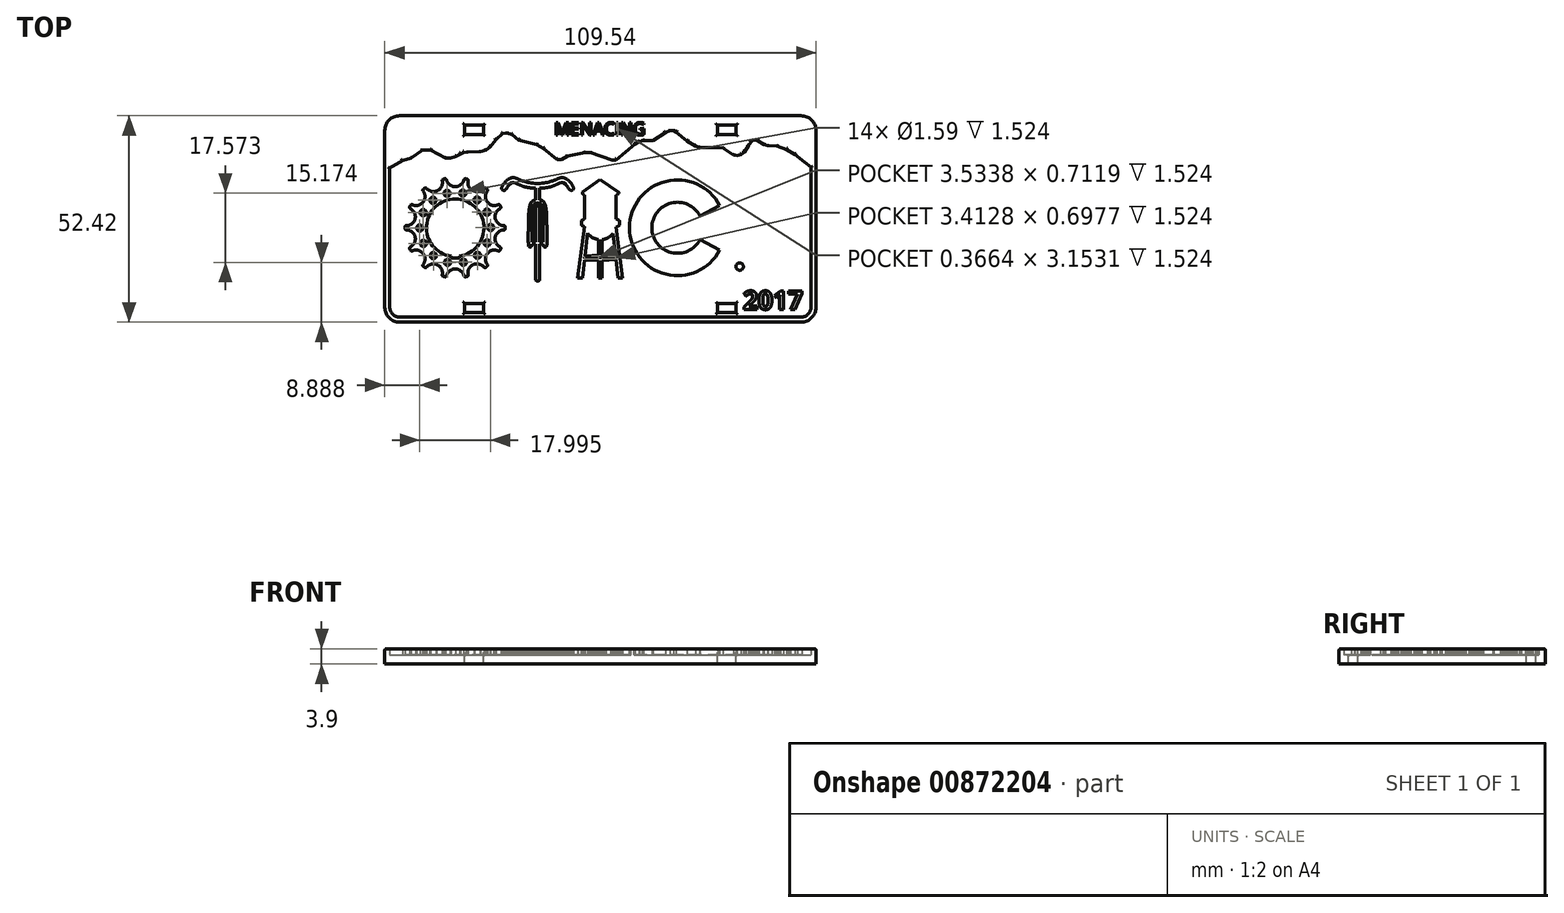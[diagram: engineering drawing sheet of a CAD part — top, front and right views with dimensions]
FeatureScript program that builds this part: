
annotation { "Feature Type Name" : "Feature", "Feature Type Description" : "" }
export const myFeature = defineFeature(function(context is Context, id is Id, definition is map)
    precondition{}
    {
        {
            var Q0;
            Q0=qCreatedBy(makeId("Top.planeOp"),FACE);
            var sketch = newSketch(context, id + "F0", { "sketchPlane" : qUnion([Q0])});
            skLineSegment(sketch, "E0", {"start": v(54.77, -22.46) * mm, "end": v(54.77, 22.46) * mm});
            skArc(sketch, "E1", {"start": v(54.77, 22.46) * mm, "mid": v(53.68, 25.11) * mm, "end": v(51.02, 26.21) * mm});
            skLineSegment(sketch, "E2", {"start": v(51.02, 26.21) * mm, "end": v(-51.02, 26.21) * mm});
            skArc(sketch, "E3", {"start": v(-51.02, 26.21) * mm, "mid": v(-53.68, 25.11) * mm, "end": v(-54.77, 22.46) * mm});
            skLineSegment(sketch, "E4", {"start": v(-54.77, 22.46) * mm, "end": v(-54.77, -22.46) * mm});
            skArc(sketch, "E5", {"start": v(-54.77, -22.46) * mm, "mid": v(-53.54, -25.24) * mm, "end": v(-50.64, -26.2) * mm});
            skLineSegment(sketch, "E6", {"start": v(-50.64, -26.2) * mm, "end": v(51.04, -26.2) * mm});
            skArc(sketch, "E7", {"start": v(51.02, -26.21) * mm, "mid": v(53.68, -25.11) * mm, "end": v(54.77, -22.46) * mm});
            skLineSegment(sketch, "E8", {"start": v(-54.77, 12.13) * mm, "end": v(-50.31, 14.84) * mm});
            skLineSegment(sketch, "E9", {"start": v(-50.31, 14.84) * mm, "end": v(-48.06, 15.4) * mm});
            skLineSegment(sketch, "E10", {"start": v(-48.06, 15.4) * mm, "end": v(-45.2, 17.44) * mm});
            skLineSegment(sketch, "E11", {"start": v(-45.2, 17.44) * mm, "end": v(-43.14, 17.44) * mm});
            skLineSegment(sketch, "E12", {"start": v(-43.14, 17.44) * mm, "end": v(-39.3, 15.5) * mm});
            skLineSegment(sketch, "E13", {"start": v(-39.3, 15.5) * mm, "end": v(-38.03, 15.49) * mm});
            skLineSegment(sketch, "E14", {"start": v(-38.03, 15.49) * mm, "end": v(-36.75, 15.8) * mm});
            skLineSegment(sketch, "E15", {"start": v(-36.75, 15.8) * mm, "end": v(-35.57, 16.54) * mm});
            skLineSegment(sketch, "E16", {"start": v(-35.57, 16.54) * mm, "end": v(-34.73, 16.88) * mm});
            skLineSegment(sketch, "E17", {"start": v(-34.73, 16.88) * mm, "end": v(-33.6, 17.01) * mm});
            skLineSegment(sketch, "E18", {"start": v(-33.6, 17.01) * mm, "end": v(-30.43, 17.11) * mm});
            skLineSegment(sketch, "E19", {"start": v(-30.43, 17.11) * mm, "end": v(-29.05, 17.5) * mm});
            skLineSegment(sketch, "E20", {"start": v(-29.05, 17.5) * mm, "end": v(-27.98, 18.27) * mm});
            skLineSegment(sketch, "E21", {"start": v(-27.98, 18.27) * mm, "end": v(-26.53, 20.14) * mm});
            skLineSegment(sketch, "E22", {"start": v(-26.53, 20.14) * mm, "end": v(-24.88, 21.63) * mm});
            skLineSegment(sketch, "E23", {"start": v(-24.88, 21.63) * mm, "end": v(-23.73, 21.77) * mm});
            skLineSegment(sketch, "E24", {"start": v(-23.73, 21.77) * mm, "end": v(-22.5, 21.4) * mm});
            skLineSegment(sketch, "E25", {"start": v(-22.5, 21.4) * mm, "end": v(-20.72, 20.04) * mm});
            skLineSegment(sketch, "E26", {"start": v(-20.72, 20.04) * mm, "end": v(-16.23, 18.87) * mm});
            skLineSegment(sketch, "E27", {"start": v(-16.23, 18.87) * mm, "end": v(-14.45, 17.85) * mm});
            skLineSegment(sketch, "E28", {"start": v(-14.45, 17.85) * mm, "end": v(-11.02, 15.1) * mm});
            skLineSegment(sketch, "E29", {"start": v(-11.02, 15.1) * mm, "end": v(-9.93, 15.1) * mm});
            skLineSegment(sketch, "E30", {"start": v(-9.93, 15.1) * mm, "end": v(-8.4, 15.96) * mm});
            skLineSegment(sketch, "E31", {"start": v(-8.4, 15.96) * mm, "end": v(-3.94, 16.85) * mm});
            skLineSegment(sketch, "E32", {"start": v(-3.94, 16.85) * mm, "end": v(-2.54, 16.85) * mm});
            skLineSegment(sketch, "E33", {"start": v(-2.54, 16.85) * mm, "end": v(2.9, 14.97) * mm});
            skLineSegment(sketch, "E34", {"start": v(2.9, 14.97) * mm, "end": v(3.92, 14.97) * mm});
            skLineSegment(sketch, "E35", {"start": v(3.92, 14.97) * mm, "end": v(8.8, 18.97) * mm});
            skLineSegment(sketch, "E36", {"start": v(8.8, 18.97) * mm, "end": v(9.82, 19.64) * mm});
            skLineSegment(sketch, "E37", {"start": v(9.82, 19.64) * mm, "end": v(10.9, 19.97) * mm});
            skLineSegment(sketch, "E38", {"start": v(10.9, 19.97) * mm, "end": v(13.43, 19.86) * mm});
            skLineSegment(sketch, "E39", {"start": v(13.43, 19.86) * mm, "end": v(16.5, 21.96) * mm});
            skLineSegment(sketch, "E40", {"start": v(16.5, 21.96) * mm, "end": v(17.71, 22.42) * mm});
            skLineSegment(sketch, "E41", {"start": v(17.71, 22.42) * mm, "end": v(18.56, 22.45) * mm});
            skLineSegment(sketch, "E42", {"start": v(18.56, 22.45) * mm, "end": v(19.28, 22.13) * mm});
            skLineSegment(sketch, "E43", {"start": v(19.28, 22.13) * mm, "end": v(22.05, 19.8) * mm});
            skLineSegment(sketch, "E44", {"start": v(22.05, 19.8) * mm, "end": v(24.2, 18.5) * mm});
            skLineSegment(sketch, "E45", {"start": v(24.2, 18.5) * mm, "end": v(25.23, 18.2) * mm});
            skLineSegment(sketch, "E46", {"start": v(25.23, 18.2) * mm, "end": v(29.85, 18.2) * mm});
            skLineSegment(sketch, "E47", {"start": v(29.85, 18.2) * mm, "end": v(31.13, 17.95) * mm});
            skLineSegment(sketch, "E48", {"start": v(31.13, 17.95) * mm, "end": v(33.84, 16.27) * mm});
            skLineSegment(sketch, "E49", {"start": v(33.84, 16.27) * mm, "end": v(34.73, 16.06) * mm});
            skLineSegment(sketch, "E50", {"start": v(34.73, 16.06) * mm, "end": v(35.67, 16.3) * mm});
            skLineSegment(sketch, "E51", {"start": v(35.67, 16.3) * mm, "end": v(36.58, 16.95) * mm});
            skLineSegment(sketch, "E52", {"start": v(36.58, 16.95) * mm, "end": v(37.58, 18.67) * mm});
            skLineSegment(sketch, "E53", {"start": v(37.58, 18.67) * mm, "end": v(38.22, 19.58) * mm});
            skLineSegment(sketch, "E54", {"start": v(38.22, 19.58) * mm, "end": v(38.96, 20.06) * mm});
            skLineSegment(sketch, "E55", {"start": v(38.96, 20.06) * mm, "end": v(39.94, 19.92) * mm});
            skLineSegment(sketch, "E56", {"start": v(39.94, 19.92) * mm, "end": v(41.58, 18.88) * mm});
            skLineSegment(sketch, "E57", {"start": v(41.58, 18.88) * mm, "end": v(42.4, 18.61) * mm});
            skLineSegment(sketch, "E58", {"start": v(42.4, 18.61) * mm, "end": v(44.9, 18.47) * mm});
            skLineSegment(sketch, "E59", {"start": v(44.9, 18.47) * mm, "end": v(47.31, 17.68) * mm});
            skLineSegment(sketch, "E60", {"start": v(47.31, 17.68) * mm, "end": v(49.47, 16.33) * mm});
            skLineSegment(sketch, "E61", {"start": v(49.47, 16.33) * mm, "end": v(51.88, 14.42) * mm});
            skLineSegment(sketch, "E62", {"start": v(51.88, 14.42) * mm, "end": v(53.78, 12.92) * mm});
            skLineSegment(sketch, "E63", {"start": v(53.78, 12.92) * mm, "end": v(54.77, 12.06) * mm});
            skArc(sketch, "E64", {"start": v(-33.82, 10.1) * mm, "mid": v(-34.05, 10.15) * mm, "end": v(-34.28, 10.2) * mm});
            skArc(sketch, "E65", {"start": v(-33.6, 9.72) * mm, "mid": v(-33.63, 9.96) * mm, "end": v(-33.82, 10.1) * mm});
            skArc(sketch, "E66", {"start": v(-39.11, 9.96) * mm, "mid": v(-36.88, 8.19) * mm, "end": v(-34.66, 9.96) * mm});
            skArc(sketch, "E67", {"start": v(-34.28, 10.2) * mm, "mid": v(-34.52, 10.16) * mm, "end": v(-34.66, 9.96) * mm});
            skArc(sketch, "E68", {"start": v(-39.49, 10.2) * mm, "mid": v(-39.72, 10.15) * mm, "end": v(-39.94, 10.1) * mm});
            skArc(sketch, "E69", {"start": v(-39.11, 9.96) * mm, "mid": v(-39.25, 10.16) * mm, "end": v(-39.49, 10.2) * mm});
            skArc(sketch, "E70", {"start": v(-44.19, 7.79) * mm, "mid": v(-41.41, 7.16) * mm, "end": v(-40.18, 9.72) * mm});
            skArc(sketch, "E71", {"start": v(-39.94, 10.1) * mm, "mid": v(-40.14, 9.96) * mm, "end": v(-40.18, 9.72) * mm});
            skArc(sketch, "E72", {"start": v(-44.63, 7.84) * mm, "mid": v(-44.82, 7.7) * mm, "end": v(-45, 7.55) * mm});
            skArc(sketch, "E73", {"start": v(-44.19, 7.79) * mm, "mid": v(-44.4, 7.9) * mm, "end": v(-44.63, 7.84) * mm});
            skArc(sketch, "E74", {"start": v(-47.82, 3.63) * mm, "mid": v(-45.05, 4.26) * mm, "end": v(-45.05, 7.1) * mm});
            skArc(sketch, "E75", {"start": v(-45, 7.55) * mm, "mid": v(-45.11, 7.34) * mm, "end": v(-45.05, 7.1) * mm});
            skArc(sketch, "E76", {"start": v(-48.24, 3.48) * mm, "mid": v(-48.35, 3.27) * mm, "end": v(-48.45, 3.06) * mm});
            skArc(sketch, "E77", {"start": v(-47.82, 3.63) * mm, "mid": v(-48.06, 3.64) * mm, "end": v(-48.24, 3.48) * mm});
            skArc(sketch, "E78", {"start": v(-49.29, -1.7) * mm, "mid": v(-47.06, 0.07) * mm, "end": v(-48.3, 2.64) * mm});
            skArc(sketch, "E79", {"start": v(-48.45, 3.06) * mm, "mid": v(-48.46, 2.82) * mm, "end": v(-48.3, 2.64) * mm});
            skArc(sketch, "E80", {"start": v(-49.6, -2.01) * mm, "mid": v(-49.6, -2.25) * mm, "end": v(-49.6, -2.48) * mm});
            skArc(sketch, "E81", {"start": v(-49.29, -1.7) * mm, "mid": v(-49.5, -1.8) * mm, "end": v(-49.6, -2.01) * mm});
            skArc(sketch, "E82", {"start": v(-48.3, -7.14) * mm, "mid": v(-47.06, -4.57) * mm, "end": v(-49.29, -2.8) * mm});
            skArc(sketch, "E83", {"start": v(-49.6, -2.48) * mm, "mid": v(-49.5, -2.7) * mm, "end": v(-49.29, -2.8) * mm});
            skArc(sketch, "E84", {"start": v(-48.45, -7.56) * mm, "mid": v(-48.35, -7.77) * mm, "end": v(-48.24, -7.98) * mm});
            skArc(sketch, "E85", {"start": v(-48.3, -7.14) * mm, "mid": v(-48.46, -7.32) * mm, "end": v(-48.45, -7.56) * mm});
            skArc(sketch, "E86", {"start": v(-45.05, -11.6) * mm, "mid": v(-45.05, -8.76) * mm, "end": v(-47.82, -8.12) * mm});
            skArc(sketch, "E87", {"start": v(-48.24, -7.98) * mm, "mid": v(-48.06, -8.14) * mm, "end": v(-47.82, -8.12) * mm});
            skArc(sketch, "E88", {"start": v(-45, -12.05) * mm, "mid": v(-44.82, -12.2) * mm, "end": v(-44.63, -12.34) * mm});
            skArc(sketch, "E89", {"start": v(-45.05, -11.6) * mm, "mid": v(-45.11, -11.84) * mm, "end": v(-45, -12.05) * mm});
            skArc(sketch, "E90", {"start": v(-40.18, -14.22) * mm, "mid": v(-41.41, -11.65) * mm, "end": v(-44.19, -12.29) * mm});
            skArc(sketch, "E91", {"start": v(-44.63, -12.34) * mm, "mid": v(-44.4, -12.4) * mm, "end": v(-44.19, -12.29) * mm});
            skArc(sketch, "E92", {"start": v(-39.94, -14.6) * mm, "mid": v(-39.72, -14.65) * mm, "end": v(-39.49, -14.7) * mm});
            skArc(sketch, "E93", {"start": v(-40.18, -14.22) * mm, "mid": v(-40.14, -14.46) * mm, "end": v(-39.94, -14.6) * mm});
            skArc(sketch, "E94", {"start": v(-34.66, -14.46) * mm, "mid": v(-36.88, -12.69) * mm, "end": v(-39.11, -14.46) * mm});
            skArc(sketch, "E95", {"start": v(-39.49, -14.7) * mm, "mid": v(-39.25, -14.66) * mm, "end": v(-39.11, -14.46) * mm});
            skArc(sketch, "E96", {"start": v(-34.28, -14.7) * mm, "mid": v(-34.05, -14.65) * mm, "end": v(-33.82, -14.6) * mm});
            skArc(sketch, "E97", {"start": v(-34.66, -14.46) * mm, "mid": v(-34.52, -14.66) * mm, "end": v(-34.28, -14.7) * mm});
            skArc(sketch, "E98", {"start": v(-29.58, -12.29) * mm, "mid": v(-32.36, -11.65) * mm, "end": v(-33.6, -14.22) * mm});
            skArc(sketch, "E99", {"start": v(-33.82, -14.6) * mm, "mid": v(-33.63, -14.46) * mm, "end": v(-33.6, -14.22) * mm});
            skArc(sketch, "E100", {"start": v(-29.14, -12.34) * mm, "mid": v(-28.95, -12.2) * mm, "end": v(-28.77, -12.05) * mm});
            skArc(sketch, "E101", {"start": v(-29.58, -12.29) * mm, "mid": v(-29.37, -12.4) * mm, "end": v(-29.14, -12.34) * mm});
            skArc(sketch, "E102", {"start": v(-25.95, -8.12) * mm, "mid": v(-28.72, -8.76) * mm, "end": v(-28.72, -11.6) * mm});
            skArc(sketch, "E103", {"start": v(-28.77, -12.05) * mm, "mid": v(-28.66, -11.84) * mm, "end": v(-28.72, -11.6) * mm});
            skArc(sketch, "E104", {"start": v(-25.53, -7.98) * mm, "mid": v(-25.42, -7.77) * mm, "end": v(-25.32, -7.56) * mm});
            skArc(sketch, "E105", {"start": v(-25.95, -8.12) * mm, "mid": v(-25.7, -8.14) * mm, "end": v(-25.53, -7.98) * mm});
            skArc(sketch, "E106", {"start": v(-24.48, -2.8) * mm, "mid": v(-26.7, -4.57) * mm, "end": v(-25.47, -7.14) * mm});
            skArc(sketch, "E107", {"start": v(-25.32, -7.56) * mm, "mid": v(-25.31, -7.32) * mm, "end": v(-25.47, -7.14) * mm});
            skArc(sketch, "E108", {"start": v(-24.16, -2.48) * mm, "mid": v(-24.16, -2.25) * mm, "end": v(-24.16, -2.01) * mm});
            skArc(sketch, "E109", {"start": v(-24.48, -2.8) * mm, "mid": v(-24.26, -2.7) * mm, "end": v(-24.16, -2.48) * mm});
            skArc(sketch, "E110", {"start": v(-25.47, 2.64) * mm, "mid": v(-26.7, 0.07) * mm, "end": v(-24.48, -1.7) * mm});
            skArc(sketch, "E111", {"start": v(-24.16, -2.01) * mm, "mid": v(-24.26, -1.8) * mm, "end": v(-24.48, -1.7) * mm});
            skArc(sketch, "E112", {"start": v(-25.32, 3.06) * mm, "mid": v(-25.42, 3.27) * mm, "end": v(-25.53, 3.48) * mm});
            skArc(sketch, "E113", {"start": v(-25.47, 2.64) * mm, "mid": v(-25.31, 2.82) * mm, "end": v(-25.32, 3.06) * mm});
            skArc(sketch, "E114", {"start": v(-28.72, 7.1) * mm, "mid": v(-28.72, 4.26) * mm, "end": v(-25.95, 3.63) * mm});
            skArc(sketch, "E115", {"start": v(-25.53, 3.48) * mm, "mid": v(-25.7, 3.64) * mm, "end": v(-25.95, 3.63) * mm});
            skArc(sketch, "E116", {"start": v(-28.77, 7.55) * mm, "mid": v(-28.95, 7.7) * mm, "end": v(-29.14, 7.84) * mm});
            skArc(sketch, "E117", {"start": v(-28.72, 7.1) * mm, "mid": v(-28.66, 7.34) * mm, "end": v(-28.77, 7.55) * mm});
            skArc(sketch, "E118", {"start": v(-33.6, 9.72) * mm, "mid": v(-32.36, 7.16) * mm, "end": v(-29.58, 7.79) * mm});
            skArc(sketch, "E119", {"start": v(-29.14, 7.84) * mm, "mid": v(-29.37, 7.9) * mm, "end": v(-29.58, 7.79) * mm});
            skArc(sketch, "E120", {"start": v(-35.84, -9.47) * mm, "mid": v(-36.88, 5.05) * mm, "end": v(-37.93, -9.47) * mm});
            skCircle(sketch, "E121", {"center": v(19.55, -2.25) * mm, "radius": 4.78 * mm});
            skLineSegment(sketch, "E122", {"start": v(25.28, 0.76) * mm, "end": v(30.31, 3.41) * mm});
            skArc(sketch, "E123", {"start": v(30.31, 3.41) * mm, "mid": v(7.4, -2.25) * mm, "end": v(30.31, -7.9) * mm});
            skLineSegment(sketch, "E124", {"start": v(25.28, -5.26) * mm, "end": v(30.31, -7.9) * mm});
            skLineSegment(sketch, "E125", {"start": v(5.68, -15.07) * mm, "end": v(3.96, -2.08) * mm});
            skLineSegment(sketch, "E126", {"start": v(4.46, -15.07) * mm, "end": v(3.92, -10.33) * mm});
            skLineSegment(sketch, "E127", {"start": v(3.83, -9.95) * mm, "end": v(3.8, -9.64) * mm});
            skLineSegment(sketch, "E128", {"start": v(3.8, -9.28) * mm, "end": v(3.17, -3.74) * mm});
            skLineSegment(sketch, "E129", {"start": v(-0.06, 10.03) * mm, "end": v(4.72, 6.75) * mm});
            skLineSegment(sketch, "E130", {"start": v(-4.58, 6.82) * mm, "end": v(-0.06, 10.03) * mm});
            skLineSegment(sketch, "E131", {"start": v(3.92, -10.33) * mm, "end": v(0.42, -10.54) * mm});
            skLineSegment(sketch, "E132", {"start": v(-0.52, -10.52) * mm, "end": v(-4.03, -10.4) * mm});
            skLineSegment(sketch, "E133", {"start": v(-3.93, -9.37) * mm, "end": v(-0.52, -9.12) * mm});
            skLineSegment(sketch, "E134", {"start": v(0.42, -9.16) * mm, "end": v(3.8, -9.28) * mm});
            skLineSegment(sketch, "E135", {"start": v(3.83, -9.95) * mm, "end": v(0.42, -10.22) * mm});
            skLineSegment(sketch, "E136", {"start": v(-0.52, -10.17) * mm, "end": v(-4.05, -10.05) * mm});
            skLineSegment(sketch, "E137", {"start": v(-4.05, -10.05) * mm, "end": v(-3.98, -9.72) * mm});
            skLineSegment(sketch, "E138", {"start": v(-3.98, -9.72) * mm, "end": v(-0.52, -9.46) * mm});
            skLineSegment(sketch, "E139", {"start": v(0.42, -9.53) * mm, "end": v(3.8, -9.64) * mm});
            skLineSegment(sketch, "E140", {"start": v(3.94, 6.03) * mm, "end": v(4.02, -0.07) * mm});
            skLineSegment(sketch, "E141", {"start": v(-3.97, 6.02) * mm, "end": v(-3.96, -0.05) * mm});
            skLineSegment(sketch, "E142", {"start": v(4.85, -0.43) * mm, "end": v(4.82, -1.6) * mm});
            skLineSegment(sketch, "E143", {"start": v(-4.82, -0.4) * mm, "end": v(-4.8, -1.63) * mm});
            skArc(sketch, "E144", {"start": v(3.94, 6.03) * mm, "mid": v(4.44, 6.27) * mm, "end": v(4.72, 6.75) * mm});
            skArc(sketch, "E145", {"start": v(-4.58, 6.82) * mm, "mid": v(-4.44, 6.3) * mm, "end": v(-3.97, 6.02) * mm});
            skArc(sketch, "E146", {"start": v(4.85, -0.43) * mm, "mid": v(4.45, -0.2) * mm, "end": v(4.02, -0.07) * mm});
            skArc(sketch, "E147", {"start": v(-3.96, -0.05) * mm, "mid": v(-4.4, -0.19) * mm, "end": v(-4.82, -0.4) * mm});
            skArc(sketch, "E148", {"start": v(-4.8, -1.63) * mm, "mid": v(-4.43, -1.8) * mm, "end": v(-4.05, -1.93) * mm});
            skArc(sketch, "E149", {"start": v(3.96, -2.08) * mm, "mid": v(4.42, -1.9) * mm, "end": v(4.82, -1.6) * mm});
            skArc(sketch, "E150", {"start": v(-3.27, -3.62) * mm, "mid": v(-2.06, -4.7) * mm, "end": v(-0.52, -5.22) * mm});
            skArc(sketch, "E151", {"start": v(0.42, -5.23) * mm, "mid": v(1.94, -4.76) * mm, "end": v(3.17, -3.74) * mm});
            skLineSegment(sketch, "E152", {"start": v(-5.8, -15.07) * mm, "end": v(-4.05, -1.93) * mm});
            skLineSegment(sketch, "E153", {"start": v(-3.93, -9.37) * mm, "end": v(-3.27, -3.62) * mm});
            skLineSegment(sketch, "E154", {"start": v(-4.56, -15.07) * mm, "end": v(-4.03, -10.4) * mm});
            skLineSegment(sketch, "E155", {"start": v(-0.52, -5.22) * mm, "end": v(-0.52, -9.12) * mm});
            skLineSegment(sketch, "E156", {"start": v(-0.52, -10.52) * mm, "end": v(-0.52, -15.07) * mm});
            skLineSegment(sketch, "E157", {"start": v(0.42, -5.23) * mm, "end": v(0.42, -9.16) * mm});
            skLineSegment(sketch, "E158", {"start": v(0.42, -10.54) * mm, "end": v(0.42, -15.07) * mm});
            skLineSegment(sketch, "E159", {"start": v(-4.56, -15.07) * mm, "end": v(-5.8, -15.07) * mm});
            skLineSegment(sketch, "E160", {"start": v(0.42, -15.07) * mm, "end": v(-0.52, -15.07) * mm});
            skLineSegment(sketch, "E161", {"start": v(5.68, -15.07) * mm, "end": v(4.46, -15.07) * mm});
            skLineSegment(sketch, "E162", {"start": v(-15.96, 9) * mm, "end": v(-16.55, 9.03) * mm});
            skLineSegment(sketch, "E163", {"start": v(-16.55, 9.03) * mm, "end": v(-17.09, 9.08) * mm});
            skLineSegment(sketch, "E164", {"start": v(-17.09, 9.08) * mm, "end": v(-17.58, 9.14) * mm});
            skLineSegment(sketch, "E165", {"start": v(-17.58, 9.14) * mm, "end": v(-18.03, 9.21) * mm});
            skLineSegment(sketch, "E166", {"start": v(-18.03, 9.21) * mm, "end": v(-18.44, 9.3) * mm});
            skLineSegment(sketch, "E167", {"start": v(-18.44, 9.3) * mm, "end": v(-18.8, 9.39) * mm});
            skLineSegment(sketch, "E168", {"start": v(-18.8, 9.39) * mm, "end": v(-19.14, 9.48) * mm});
            skLineSegment(sketch, "E169", {"start": v(-19.14, 9.48) * mm, "end": v(-19.45, 9.57) * mm});
            skLineSegment(sketch, "E170", {"start": v(-19.45, 9.57) * mm, "end": v(-19.73, 9.67) * mm});
            skLineSegment(sketch, "E171", {"start": v(-19.73, 9.67) * mm, "end": v(-19.99, 9.76) * mm});
            skLineSegment(sketch, "E172", {"start": v(-19.99, 9.76) * mm, "end": v(-20.22, 9.85) * mm});
            skLineSegment(sketch, "E173", {"start": v(-20.22, 9.85) * mm, "end": v(-20.43, 9.93) * mm});
            skLineSegment(sketch, "E174", {"start": v(-20.43, 9.93) * mm, "end": v(-20.62, 10.01) * mm});
            skLineSegment(sketch, "E175", {"start": v(-20.62, 10.01) * mm, "end": v(-20.79, 10.09) * mm});
            skLineSegment(sketch, "E176", {"start": v(-20.79, 10.09) * mm, "end": v(-20.94, 10.15) * mm});
            skLineSegment(sketch, "E177", {"start": v(-20.94, 10.15) * mm, "end": v(-21.08, 10.22) * mm});
            skLineSegment(sketch, "E178", {"start": v(-21.08, 10.22) * mm, "end": v(-21.2, 10.27) * mm});
            skLineSegment(sketch, "E179", {"start": v(-21.2, 10.27) * mm, "end": v(-21.32, 10.32) * mm});
            skLineSegment(sketch, "E180", {"start": v(-21.32, 10.32) * mm, "end": v(-21.43, 10.35) * mm});
            skLineSegment(sketch, "E181", {"start": v(-21.43, 10.35) * mm, "end": v(-21.52, 10.39) * mm});
            skLineSegment(sketch, "E182", {"start": v(-21.52, 10.39) * mm, "end": v(-21.61, 10.42) * mm});
            skLineSegment(sketch, "E183", {"start": v(-21.61, 10.42) * mm, "end": v(-21.7, 10.44) * mm});
            skLineSegment(sketch, "E184", {"start": v(-21.7, 10.44) * mm, "end": v(-21.77, 10.46) * mm});
            skLineSegment(sketch, "E185", {"start": v(-21.77, 10.46) * mm, "end": v(-21.85, 10.47) * mm});
            skLineSegment(sketch, "E186", {"start": v(-21.85, 10.47) * mm, "end": v(-21.93, 10.48) * mm});
            skLineSegment(sketch, "E187", {"start": v(-21.93, 10.48) * mm, "end": v(-22, 10.5) * mm});
            skLineSegment(sketch, "E188", {"start": v(-22, 10.5) * mm, "end": v(-22.08, 10.5) * mm});
            skLineSegment(sketch, "E189", {"start": v(-22.08, 10.5) * mm, "end": v(-22.15, 10.5) * mm});
            skLineSegment(sketch, "E190", {"start": v(-22.15, 10.5) * mm, "end": v(-22.23, 10.5) * mm});
            skLineSegment(sketch, "E191", {"start": v(-22.23, 10.5) * mm, "end": v(-22.3, 10.5) * mm});
            skLineSegment(sketch, "E192", {"start": v(-22.3, 10.5) * mm, "end": v(-22.38, 10.48) * mm});
            skLineSegment(sketch, "E193", {"start": v(-22.38, 10.48) * mm, "end": v(-22.46, 10.47) * mm});
            skLineSegment(sketch, "E194", {"start": v(-22.46, 10.47) * mm, "end": v(-22.54, 10.46) * mm});
            skLineSegment(sketch, "E195", {"start": v(-22.54, 10.46) * mm, "end": v(-22.63, 10.44) * mm});
            skLineSegment(sketch, "E196", {"start": v(-22.63, 10.44) * mm, "end": v(-22.71, 10.41) * mm});
            skLineSegment(sketch, "E197", {"start": v(-22.71, 10.41) * mm, "end": v(-22.8, 10.39) * mm});
            skLineSegment(sketch, "E198", {"start": v(-22.8, 10.39) * mm, "end": v(-22.88, 10.36) * mm});
            skLineSegment(sketch, "E199", {"start": v(-22.88, 10.36) * mm, "end": v(-22.97, 10.32) * mm});
            skLineSegment(sketch, "E200", {"start": v(-22.97, 10.32) * mm, "end": v(-23.05, 10.28) * mm});
            skLineSegment(sketch, "E201", {"start": v(-23.05, 10.28) * mm, "end": v(-23.14, 10.24) * mm});
            skLineSegment(sketch, "E202", {"start": v(-23.14, 10.24) * mm, "end": v(-23.23, 10.2) * mm});
            skLineSegment(sketch, "E203", {"start": v(-23.23, 10.2) * mm, "end": v(-23.31, 10.14) * mm});
            skLineSegment(sketch, "E204", {"start": v(-23.31, 10.14) * mm, "end": v(-23.4, 10.09) * mm});
            skLineSegment(sketch, "E205", {"start": v(-23.4, 10.09) * mm, "end": v(-23.48, 10.03) * mm});
            skLineSegment(sketch, "E206", {"start": v(-23.48, 10.03) * mm, "end": v(-23.57, 9.97) * mm});
            skLineSegment(sketch, "E207", {"start": v(-23.57, 9.97) * mm, "end": v(-23.65, 9.9) * mm});
            skLineSegment(sketch, "E208", {"start": v(-23.65, 9.9) * mm, "end": v(-23.74, 9.83) * mm});
            skLineSegment(sketch, "E209", {"start": v(-23.74, 9.83) * mm, "end": v(-23.82, 9.76) * mm});
            skLineSegment(sketch, "E210", {"start": v(-23.82, 9.76) * mm, "end": v(-23.9, 9.7) * mm});
            skLineSegment(sketch, "E211", {"start": v(-23.9, 9.7) * mm, "end": v(-23.98, 9.62) * mm});
            skLineSegment(sketch, "E212", {"start": v(-23.98, 9.62) * mm, "end": v(-24.05, 9.54) * mm});
            skLineSegment(sketch, "E213", {"start": v(-24.05, 9.54) * mm, "end": v(-24.13, 9.45) * mm});
            skLineSegment(sketch, "E214", {"start": v(-24.13, 9.45) * mm, "end": v(-24.2, 9.36) * mm});
            skLineSegment(sketch, "E215", {"start": v(-24.2, 9.36) * mm, "end": v(-24.29, 9.27) * mm});
            skLineSegment(sketch, "E216", {"start": v(-24.29, 9.27) * mm, "end": v(-24.37, 9.17) * mm});
            skLineSegment(sketch, "E217", {"start": v(-24.37, 9.17) * mm, "end": v(-24.45, 9.06) * mm});
            skLineSegment(sketch, "E218", {"start": v(-24.45, 9.06) * mm, "end": v(-24.53, 8.94) * mm});
            skLineSegment(sketch, "E219", {"start": v(-24.53, 8.94) * mm, "end": v(-24.61, 8.82) * mm});
            skLineSegment(sketch, "E220", {"start": v(-24.61, 8.82) * mm, "end": v(-24.7, 8.7) * mm});
            skLineSegment(sketch, "E221", {"start": v(-24.7, 8.7) * mm, "end": v(-24.77, 8.57) * mm});
            skLineSegment(sketch, "E222", {"start": v(-24.77, 8.57) * mm, "end": v(-24.84, 8.45) * mm});
            skLineSegment(sketch, "E223", {"start": v(-24.84, 8.45) * mm, "end": v(-24.9, 8.33) * mm});
            skLineSegment(sketch, "E224", {"start": v(-24.9, 8.33) * mm, "end": v(-24.97, 8.22) * mm});
            skLineSegment(sketch, "E225", {"start": v(-24.97, 8.22) * mm, "end": v(-25.01, 8.11) * mm});
            skLineSegment(sketch, "E226", {"start": v(-25.01, 8.11) * mm, "end": v(-25.05, 8.02) * mm});
            skLineSegment(sketch, "E227", {"start": v(-25.05, 8.02) * mm, "end": v(-25.08, 7.94) * mm});
            skLineSegment(sketch, "E228", {"start": v(-25.08, 7.94) * mm, "end": v(-25.1, 7.87) * mm});
            skLineSegment(sketch, "E229", {"start": v(-25.1, 7.87) * mm, "end": v(-25.1, 7.8) * mm});
            skLineSegment(sketch, "E230", {"start": v(-25.1, 7.8) * mm, "end": v(-25.1, 7.74) * mm});
            skLineSegment(sketch, "E231", {"start": v(-25.1, 7.74) * mm, "end": v(-25.1, 7.7) * mm});
            skLineSegment(sketch, "E232", {"start": v(-25.1, 7.7) * mm, "end": v(-25.08, 7.64) * mm});
            skLineSegment(sketch, "E233", {"start": v(-25.08, 7.64) * mm, "end": v(-25.06, 7.6) * mm});
            skLineSegment(sketch, "E234", {"start": v(-25.06, 7.6) * mm, "end": v(-25.04, 7.55) * mm});
            skLineSegment(sketch, "E235", {"start": v(-25.04, 7.55) * mm, "end": v(-25, 7.5) * mm});
            skLineSegment(sketch, "E236", {"start": v(-25, 7.5) * mm, "end": v(-24.98, 7.47) * mm});
            skLineSegment(sketch, "E237", {"start": v(-24.98, 7.47) * mm, "end": v(-24.94, 7.43) * mm});
            skLineSegment(sketch, "E238", {"start": v(-24.94, 7.43) * mm, "end": v(-24.9, 7.4) * mm});
            skLineSegment(sketch, "E239", {"start": v(-24.9, 7.4) * mm, "end": v(-24.87, 7.36) * mm});
            skLineSegment(sketch, "E240", {"start": v(-24.87, 7.36) * mm, "end": v(-24.82, 7.34) * mm});
            skLineSegment(sketch, "E241", {"start": v(-24.82, 7.34) * mm, "end": v(-24.78, 7.31) * mm});
            skLineSegment(sketch, "E242", {"start": v(-24.78, 7.31) * mm, "end": v(-24.73, 7.3) * mm});
            skLineSegment(sketch, "E243", {"start": v(-24.73, 7.3) * mm, "end": v(-24.68, 7.28) * mm});
            skLineSegment(sketch, "E244", {"start": v(-24.68, 7.28) * mm, "end": v(-24.64, 7.27) * mm});
            skLineSegment(sketch, "E245", {"start": v(-24.64, 7.27) * mm, "end": v(-24.59, 7.26) * mm});
            skLineSegment(sketch, "E246", {"start": v(-24.59, 7.26) * mm, "end": v(-24.54, 7.26) * mm});
            skLineSegment(sketch, "E247", {"start": v(-24.54, 7.26) * mm, "end": v(-24.5, 7.26) * mm});
            skLineSegment(sketch, "E248", {"start": v(-24.5, 7.26) * mm, "end": v(-24.44, 7.26) * mm});
            skLineSegment(sketch, "E249", {"start": v(-24.44, 7.26) * mm, "end": v(-24.4, 7.27) * mm});
            skLineSegment(sketch, "E250", {"start": v(-24.4, 7.27) * mm, "end": v(-24.35, 7.28) * mm});
            skLineSegment(sketch, "E251", {"start": v(-24.35, 7.28) * mm, "end": v(-24.3, 7.3) * mm});
            skLineSegment(sketch, "E252", {"start": v(-24.3, 7.3) * mm, "end": v(-24.27, 7.3) * mm});
            skLineSegment(sketch, "E253", {"start": v(-24.27, 7.3) * mm, "end": v(-24.22, 7.33) * mm});
            skLineSegment(sketch, "E254", {"start": v(-24.22, 7.33) * mm, "end": v(-24.18, 7.36) * mm});
            skLineSegment(sketch, "E255", {"start": v(-24.18, 7.36) * mm, "end": v(-24.14, 7.4) * mm});
            skLineSegment(sketch, "E256", {"start": v(-24.14, 7.4) * mm, "end": v(-24.1, 7.43) * mm});
            skLineSegment(sketch, "E257", {"start": v(-24.1, 7.43) * mm, "end": v(-24.06, 7.48) * mm});
            skLineSegment(sketch, "E258", {"start": v(-24.06, 7.48) * mm, "end": v(-24.02, 7.53) * mm});
            skLineSegment(sketch, "E259", {"start": v(-24.02, 7.53) * mm, "end": v(-23.97, 7.59) * mm});
            skLineSegment(sketch, "E260", {"start": v(-23.97, 7.59) * mm, "end": v(-23.93, 7.65) * mm});
            skLineSegment(sketch, "E261", {"start": v(-23.93, 7.65) * mm, "end": v(-23.88, 7.72) * mm});
            skLineSegment(sketch, "E262", {"start": v(-23.88, 7.72) * mm, "end": v(-23.83, 7.8) * mm});
            skLineSegment(sketch, "E263", {"start": v(-23.83, 7.8) * mm, "end": v(-23.78, 7.87) * mm});
            skLineSegment(sketch, "E264", {"start": v(-23.78, 7.87) * mm, "end": v(-23.72, 7.96) * mm});
            skLineSegment(sketch, "E265", {"start": v(-23.72, 7.96) * mm, "end": v(-23.67, 8.04) * mm});
            skLineSegment(sketch, "E266", {"start": v(-23.67, 8.04) * mm, "end": v(-23.6, 8.13) * mm});
            skLineSegment(sketch, "E267", {"start": v(-23.6, 8.13) * mm, "end": v(-23.54, 8.23) * mm});
            skLineSegment(sketch, "E268", {"start": v(-23.54, 8.23) * mm, "end": v(-23.47, 8.32) * mm});
            skLineSegment(sketch, "E269", {"start": v(-23.47, 8.32) * mm, "end": v(-23.4, 8.41) * mm});
            skLineSegment(sketch, "E270", {"start": v(-23.4, 8.41) * mm, "end": v(-23.32, 8.5) * mm});
            skLineSegment(sketch, "E271", {"start": v(-23.32, 8.5) * mm, "end": v(-23.25, 8.6) * mm});
            skLineSegment(sketch, "E272", {"start": v(-23.25, 8.6) * mm, "end": v(-23.17, 8.68) * mm});
            skLineSegment(sketch, "E273", {"start": v(-23.17, 8.68) * mm, "end": v(-23.1, 8.76) * mm});
            skLineSegment(sketch, "E274", {"start": v(-23.1, 8.76) * mm, "end": v(-23.01, 8.83) * mm});
            skLineSegment(sketch, "E275", {"start": v(-23.01, 8.83) * mm, "end": v(-22.94, 8.9) * mm});
            skLineSegment(sketch, "E276", {"start": v(-22.94, 8.9) * mm, "end": v(-22.86, 8.97) * mm});
            skLineSegment(sketch, "E277", {"start": v(-22.86, 8.97) * mm, "end": v(-22.78, 9.02) * mm});
            skLineSegment(sketch, "E278", {"start": v(-22.78, 9.02) * mm, "end": v(-22.71, 9.08) * mm});
            skLineSegment(sketch, "E279", {"start": v(-22.71, 9.08) * mm, "end": v(-22.64, 9.12) * mm});
            skLineSegment(sketch, "E280", {"start": v(-22.64, 9.12) * mm, "end": v(-22.57, 9.16) * mm});
            skLineSegment(sketch, "E281", {"start": v(-22.57, 9.16) * mm, "end": v(-22.5, 9.2) * mm});
            skLineSegment(sketch, "E282", {"start": v(-22.5, 9.2) * mm, "end": v(-22.44, 9.22) * mm});
            skLineSegment(sketch, "E283", {"start": v(-22.44, 9.22) * mm, "end": v(-22.37, 9.24) * mm});
            skLineSegment(sketch, "E284", {"start": v(-22.37, 9.24) * mm, "end": v(-22.31, 9.25) * mm});
            skLineSegment(sketch, "E285", {"start": v(-22.31, 9.25) * mm, "end": v(-22.26, 9.26) * mm});
            skLineSegment(sketch, "E286", {"start": v(-22.26, 9.26) * mm, "end": v(-22.2, 9.27) * mm});
            skLineSegment(sketch, "E287", {"start": v(-22.2, 9.27) * mm, "end": v(-22.14, 9.27) * mm});
            skLineSegment(sketch, "E288", {"start": v(-22.14, 9.27) * mm, "end": v(-22.09, 9.26) * mm});
            skLineSegment(sketch, "E289", {"start": v(-22.09, 9.26) * mm, "end": v(-22.03, 9.26) * mm});
            skLineSegment(sketch, "E290", {"start": v(-22.03, 9.26) * mm, "end": v(-21.97, 9.25) * mm});
            skLineSegment(sketch, "E291", {"start": v(-21.97, 9.25) * mm, "end": v(-21.92, 9.24) * mm});
            skLineSegment(sketch, "E292", {"start": v(-21.92, 9.24) * mm, "end": v(-21.86, 9.22) * mm});
            skLineSegment(sketch, "E293", {"start": v(-21.86, 9.22) * mm, "end": v(-21.8, 9.2) * mm});
            skLineSegment(sketch, "E294", {"start": v(-21.8, 9.2) * mm, "end": v(-21.72, 9.18) * mm});
            skLineSegment(sketch, "E295", {"start": v(-21.72, 9.18) * mm, "end": v(-21.64, 9.15) * mm});
            skLineSegment(sketch, "E296", {"start": v(-21.64, 9.15) * mm, "end": v(-21.56, 9.12) * mm});
            skLineSegment(sketch, "E297", {"start": v(-21.56, 9.12) * mm, "end": v(-21.47, 9.08) * mm});
            skLineSegment(sketch, "E298", {"start": v(-21.47, 9.08) * mm, "end": v(-21.37, 9.03) * mm});
            skLineSegment(sketch, "E299", {"start": v(-21.37, 9.03) * mm, "end": v(-21.26, 8.98) * mm});
            skLineSegment(sketch, "E300", {"start": v(-21.26, 8.98) * mm, "end": v(-21.14, 8.93) * mm});
            skLineSegment(sketch, "E301", {"start": v(-21.14, 8.93) * mm, "end": v(-21.01, 8.87) * mm});
            skLineSegment(sketch, "E302", {"start": v(-21.01, 8.87) * mm, "end": v(-20.88, 8.8) * mm});
            skLineSegment(sketch, "E303", {"start": v(-20.88, 8.8) * mm, "end": v(-20.75, 8.75) * mm});
            skLineSegment(sketch, "E304", {"start": v(-20.75, 8.75) * mm, "end": v(-20.62, 8.68) * mm});
            skLineSegment(sketch, "E305", {"start": v(-20.62, 8.68) * mm, "end": v(-20.48, 8.62) * mm});
            skLineSegment(sketch, "E306", {"start": v(-20.48, 8.62) * mm, "end": v(-20.34, 8.56) * mm});
            skLineSegment(sketch, "E307", {"start": v(-20.34, 8.56) * mm, "end": v(-20.2, 8.5) * mm});
            skLineSegment(sketch, "E308", {"start": v(-20.2, 8.5) * mm, "end": v(-20.06, 8.45) * mm});
            skLineSegment(sketch, "E309", {"start": v(-20.06, 8.45) * mm, "end": v(-19.92, 8.4) * mm});
            skLineSegment(sketch, "E310", {"start": v(-19.92, 8.4) * mm, "end": v(-19.78, 8.34) * mm});
            skLineSegment(sketch, "E311", {"start": v(-19.78, 8.34) * mm, "end": v(-19.63, 8.29) * mm});
            skLineSegment(sketch, "E312", {"start": v(-19.63, 8.29) * mm, "end": v(-19.5, 8.24) * mm});
            skLineSegment(sketch, "E313", {"start": v(-19.5, 8.24) * mm, "end": v(-19.34, 8.2) * mm});
            skLineSegment(sketch, "E314", {"start": v(-19.34, 8.2) * mm, "end": v(-19.2, 8.15) * mm});
            skLineSegment(sketch, "E315", {"start": v(-19.2, 8.15) * mm, "end": v(-19.05, 8.11) * mm});
            skLineSegment(sketch, "E316", {"start": v(-19.05, 8.11) * mm, "end": v(-18.9, 8.07) * mm});
            skLineSegment(sketch, "E317", {"start": v(-18.9, 8.07) * mm, "end": v(-18.73, 8.04) * mm});
            skLineSegment(sketch, "E318", {"start": v(-18.73, 8.04) * mm, "end": v(-18.56, 8) * mm});
            skLineSegment(sketch, "E319", {"start": v(-18.56, 8) * mm, "end": v(-18.38, 7.98) * mm});
            skLineSegment(sketch, "E320", {"start": v(-18.38, 7.98) * mm, "end": v(-18.2, 7.95) * mm});
            skLineSegment(sketch, "E321", {"start": v(-18.2, 7.95) * mm, "end": v(-18, 7.92) * mm});
            skLineSegment(sketch, "E322", {"start": v(-18, 7.92) * mm, "end": v(-17.8, 7.9) * mm});
            skLineSegment(sketch, "E323", {"start": v(-17.8, 7.9) * mm, "end": v(-17.58, 7.87) * mm});
            skLineSegment(sketch, "E324", {"start": v(-17.58, 7.87) * mm, "end": v(-17.36, 7.85) * mm});
            skLineSegment(sketch, "E325", {"start": v(-17.36, 7.85) * mm, "end": v(-17.15, 7.83) * mm});
            skLineSegment(sketch, "E326", {"start": v(-17.15, 7.83) * mm, "end": v(-16.96, 7.8) * mm});
            skLineSegment(sketch, "E327", {"start": v(-16.96, 7.8) * mm, "end": v(-16.78, 7.8) * mm});
            skLineSegment(sketch, "E328", {"start": v(-16.78, 7.8) * mm, "end": v(-16.63, 7.79) * mm});
            skLineSegment(sketch, "E329", {"start": v(-16.63, 7.79) * mm, "end": v(-16.5, 7.78) * mm});
            skLineSegment(sketch, "E330", {"start": v(-16.5, 7.78) * mm, "end": v(-17.6, 9.06) * mm});
            skLineSegment(sketch, "E331", {"start": v(-17.6, 9.06) * mm, "end": v(-19.73, 9.59) * mm});
            skLineSegment(sketch, "E332", {"start": v(-19.73, 9.59) * mm, "end": v(-21.23, 10.3) * mm});
            skLineSegment(sketch, "E333", {"start": v(-21.23, 10.3) * mm, "end": v(-21.86, 10.5) * mm});
            skLineSegment(sketch, "E334", {"start": v(-21.86, 10.5) * mm, "end": v(-22.45, 10.5) * mm});
            skLineSegment(sketch, "E335", {"start": v(-22.45, 10.5) * mm, "end": v(-23.14, 10.29) * mm});
            skLineSegment(sketch, "E336", {"start": v(-23.14, 10.29) * mm, "end": v(-23.83, 9.79) * mm});
            skLineSegment(sketch, "E337", {"start": v(-23.83, 9.79) * mm, "end": v(-24.43, 9.14) * mm});
            skLineSegment(sketch, "E338", {"start": v(-24.43, 9.14) * mm, "end": v(-25.14, 7.99) * mm});
            skLineSegment(sketch, "E339", {"start": v(-25.14, 7.99) * mm, "end": v(-25.1, 7.58) * mm});
            skLineSegment(sketch, "E340", {"start": v(-25.1, 7.58) * mm, "end": v(-24.8, 7.26) * mm});
            skLineSegment(sketch, "E341", {"start": v(-24.8, 7.26) * mm, "end": v(-24.38, 7.23) * mm});
            skLineSegment(sketch, "E342", {"start": v(-24.38, 7.23) * mm, "end": v(-24.07, 7.4) * mm});
            skLineSegment(sketch, "E343", {"start": v(-24.07, 7.4) * mm, "end": v(-23.7, 8.01) * mm});
            skLineSegment(sketch, "E344", {"start": v(-23.7, 8.01) * mm, "end": v(-23.1, 8.82) * mm});
            skLineSegment(sketch, "E345", {"start": v(-23.1, 8.82) * mm, "end": v(-22.47, 9.26) * mm});
            skLineSegment(sketch, "E346", {"start": v(-22.47, 9.26) * mm, "end": v(-22.04, 9.29) * mm});
            skLineSegment(sketch, "E347", {"start": v(-22.04, 9.29) * mm, "end": v(-21.57, 9.14) * mm});
            skLineSegment(sketch, "E348", {"start": v(-21.57, 9.14) * mm, "end": v(-20.48, 8.6) * mm});
            skLineSegment(sketch, "E349", {"start": v(-20.48, 8.6) * mm, "end": v(-19.36, 8.16) * mm});
            skLineSegment(sketch, "E350", {"start": v(-19.36, 8.16) * mm, "end": v(-18.13, 7.9) * mm});
            skLineSegment(sketch, "E351", {"start": v(-18.13, 7.9) * mm, "end": v(-16.78, 7.79) * mm});
            skLineSegment(sketch, "E352", {"start": v(-16.78, 7.79) * mm, "end": v(-16.5, 7.78) * mm});
            skLineSegment(sketch, "E353", {"start": v(-16.5, -15.31) * mm, "end": v(-16.5, -6.33) * mm});
            skLineSegment(sketch, "E354", {"start": v(-16.5, -6.33) * mm, "end": v(-17.39, -6.33) * mm});
            skLineSegment(sketch, "E355", {"start": v(-17.39, -6.33) * mm, "end": v(-17.4, -6.48) * mm});
            skLineSegment(sketch, "E356", {"start": v(-17.4, -6.48) * mm, "end": v(-17.4, -6.68) * mm});
            skLineSegment(sketch, "E357", {"start": v(-17.4, -6.68) * mm, "end": v(-17.43, -6.82) * mm});
            skLineSegment(sketch, "E358", {"start": v(-17.43, -6.82) * mm, "end": v(-17.45, -6.92) * mm});
            skLineSegment(sketch, "E359", {"start": v(-17.45, -6.92) * mm, "end": v(-17.48, -6.98) * mm});
            skLineSegment(sketch, "E360", {"start": v(-17.48, -6.98) * mm, "end": v(-17.5, -7.02) * mm});
            skLineSegment(sketch, "E361", {"start": v(-17.5, -7.02) * mm, "end": v(-17.54, -7.04) * mm});
            skLineSegment(sketch, "E362", {"start": v(-17.54, -7.04) * mm, "end": v(-17.57, -7.06) * mm});
            skLineSegment(sketch, "E363", {"start": v(-17.57, -7.06) * mm, "end": v(-17.6, -7.08) * mm});
            skLineSegment(sketch, "E364", {"start": v(-17.6, -7.08) * mm, "end": v(-17.64, -7.1) * mm});
            skLineSegment(sketch, "E365", {"start": v(-17.64, -7.1) * mm, "end": v(-17.68, -7.11) * mm});
            skLineSegment(sketch, "E366", {"start": v(-17.68, -7.11) * mm, "end": v(-17.72, -7.12) * mm});
            skLineSegment(sketch, "E367", {"start": v(-17.72, -7.12) * mm, "end": v(-17.76, -7.13) * mm});
            skLineSegment(sketch, "E368", {"start": v(-17.76, -7.13) * mm, "end": v(-17.8, -7.13) * mm});
            skLineSegment(sketch, "E369", {"start": v(-17.8, -7.13) * mm, "end": v(-17.85, -7.13) * mm});
            skLineSegment(sketch, "E370", {"start": v(-17.85, -7.13) * mm, "end": v(-17.89, -7.13) * mm});
            skLineSegment(sketch, "E371", {"start": v(-17.89, -7.13) * mm, "end": v(-17.93, -7.12) * mm});
            skLineSegment(sketch, "E372", {"start": v(-17.93, -7.12) * mm, "end": v(-17.97, -7.11) * mm});
            skLineSegment(sketch, "E373", {"start": v(-17.97, -7.11) * mm, "end": v(-18.01, -7.1) * mm});
            skLineSegment(sketch, "E374", {"start": v(-18.01, -7.1) * mm, "end": v(-18.05, -7.09) * mm});
            skLineSegment(sketch, "E375", {"start": v(-18.05, -7.09) * mm, "end": v(-18.1, -7.07) * mm});
            skLineSegment(sketch, "E376", {"start": v(-18.1, -7.07) * mm, "end": v(-18.13, -7.05) * mm});
            skLineSegment(sketch, "E377", {"start": v(-18.13, -7.05) * mm, "end": v(-18.16, -7.03) * mm});
            skLineSegment(sketch, "E378", {"start": v(-18.16, -7.03) * mm, "end": v(-18.19, -7) * mm});
            skLineSegment(sketch, "E379", {"start": v(-18.19, -7) * mm, "end": v(-18.21, -6.97) * mm});
            skLineSegment(sketch, "E380", {"start": v(-18.21, -6.97) * mm, "end": v(-18.24, -6.91) * mm});
            skLineSegment(sketch, "E381", {"start": v(-18.24, -6.91) * mm, "end": v(-18.26, -6.83) * mm});
            skLineSegment(sketch, "E382", {"start": v(-18.26, -6.83) * mm, "end": v(-18.28, -6.72) * mm});
            skLineSegment(sketch, "E383", {"start": v(-18.28, -6.72) * mm, "end": v(-18.29, -6.57) * mm});
            skLineSegment(sketch, "E384", {"start": v(-18.29, -6.57) * mm, "end": v(-18.3, -6.37) * mm});
            skLineSegment(sketch, "E385", {"start": v(-18.3, -6.37) * mm, "end": v(-18.31, -6.1) * mm});
            skLineSegment(sketch, "E386", {"start": v(-18.31, -6.1) * mm, "end": v(-18.32, -5.8) * mm});
            skLineSegment(sketch, "E387", {"start": v(-18.32, -5.8) * mm, "end": v(-18.32, -5.42) * mm});
            skLineSegment(sketch, "E388", {"start": v(-18.32, -5.42) * mm, "end": v(-18.33, -5) * mm});
            skLineSegment(sketch, "E389", {"start": v(-18.33, -5) * mm, "end": v(-18.33, -4.53) * mm});
            skLineSegment(sketch, "E390", {"start": v(-18.33, -4.53) * mm, "end": v(-18.32, -4.03) * mm});
            skLineSegment(sketch, "E391", {"start": v(-18.32, -4.03) * mm, "end": v(-18.32, -3.5) * mm});
            skLineSegment(sketch, "E392", {"start": v(-18.32, -3.5) * mm, "end": v(-18.31, -2.96) * mm});
            skLineSegment(sketch, "E393", {"start": v(-18.31, -2.96) * mm, "end": v(-18.3, -2.4) * mm});
            skLineSegment(sketch, "E394", {"start": v(-18.3, -2.4) * mm, "end": v(-18.3, -1.84) * mm});
            skLineSegment(sketch, "E395", {"start": v(-18.3, -1.84) * mm, "end": v(-18.28, -1.28) * mm});
            skLineSegment(sketch, "E396", {"start": v(-18.28, -1.28) * mm, "end": v(-18.27, -0.72) * mm});
            skLineSegment(sketch, "E397", {"start": v(-18.27, -0.72) * mm, "end": v(-18.25, -0.18) * mm});
            skLineSegment(sketch, "E398", {"start": v(-18.25, -0.18) * mm, "end": v(-18.23, 0.34) * mm});
            skLineSegment(sketch, "E399", {"start": v(-18.23, 0.34) * mm, "end": v(-18.21, 0.83) * mm});
            skLineSegment(sketch, "E400", {"start": v(-18.21, 0.83) * mm, "end": v(-18.19, 1.3) * mm});
            skLineSegment(sketch, "E401", {"start": v(-18.19, 1.3) * mm, "end": v(-18.16, 1.72) * mm});
            skLineSegment(sketch, "E402", {"start": v(-18.16, 1.72) * mm, "end": v(-18.13, 2.1) * mm});
            skLineSegment(sketch, "E403", {"start": v(-18.13, 2.1) * mm, "end": v(-18.1, 2.44) * mm});
            skLineSegment(sketch, "E404", {"start": v(-18.1, 2.44) * mm, "end": v(-18.06, 2.74) * mm});
            skLineSegment(sketch, "E405", {"start": v(-18.06, 2.74) * mm, "end": v(-18.01, 3) * mm});
            skLineSegment(sketch, "E406", {"start": v(-18.01, 3) * mm, "end": v(-17.97, 3.24) * mm});
            skLineSegment(sketch, "E407", {"start": v(-17.97, 3.24) * mm, "end": v(-17.92, 3.45) * mm});
            skLineSegment(sketch, "E408", {"start": v(-17.92, 3.45) * mm, "end": v(-17.86, 3.64) * mm});
            skLineSegment(sketch, "E409", {"start": v(-17.86, 3.64) * mm, "end": v(-17.8, 3.8) * mm});
            skLineSegment(sketch, "E410", {"start": v(-17.8, 3.8) * mm, "end": v(-17.75, 3.95) * mm});
            skLineSegment(sketch, "E411", {"start": v(-17.75, 3.95) * mm, "end": v(-17.68, 4.08) * mm});
            skLineSegment(sketch, "E412", {"start": v(-17.68, 4.08) * mm, "end": v(-17.61, 4.2) * mm});
            skLineSegment(sketch, "E413", {"start": v(-17.61, 4.2) * mm, "end": v(-17.54, 4.3) * mm});
            skLineSegment(sketch, "E414", {"start": v(-17.54, 4.3) * mm, "end": v(-17.47, 4.39) * mm});
            skLineSegment(sketch, "E415", {"start": v(-17.47, 4.39) * mm, "end": v(-17.4, 4.46) * mm});
            skLineSegment(sketch, "E416", {"start": v(-17.4, 4.46) * mm, "end": v(-17.32, 4.53) * mm});
            skLineSegment(sketch, "E417", {"start": v(-17.32, 4.53) * mm, "end": v(-17.24, 4.6) * mm});
            skLineSegment(sketch, "E418", {"start": v(-17.24, 4.6) * mm, "end": v(-17.16, 4.65) * mm});
            skLineSegment(sketch, "E419", {"start": v(-17.16, 4.65) * mm, "end": v(-17.07, 4.7) * mm});
            skLineSegment(sketch, "E420", {"start": v(-17.07, 4.7) * mm, "end": v(-16.98, 4.73) * mm});
            skLineSegment(sketch, "E421", {"start": v(-16.98, 4.73) * mm, "end": v(-16.9, 4.76) * mm});
            skLineSegment(sketch, "E422", {"start": v(-16.9, 4.76) * mm, "end": v(-16.8, 4.79) * mm});
            skLineSegment(sketch, "E423", {"start": v(-16.8, 4.79) * mm, "end": v(-16.5, 4.85) * mm});
            skLineSegment(sketch, "E424", {"start": v(-16.5, 4.85) * mm, "end": v(-16.5, 7.78) * mm});
            skLineSegment(sketch, "E425", {"start": v(-15.95, 3.98) * mm, "end": v(-16.16, 3.98) * mm});
            skLineSegment(sketch, "E426", {"start": v(-16.16, 3.98) * mm, "end": v(-16.34, 3.97) * mm});
            skLineSegment(sketch, "E427", {"start": v(-16.34, 3.97) * mm, "end": v(-16.48, 3.96) * mm});
            skLineSegment(sketch, "E428", {"start": v(-16.48, 3.96) * mm, "end": v(-16.59, 3.94) * mm});
            skLineSegment(sketch, "E429", {"start": v(-16.59, 3.94) * mm, "end": v(-16.67, 3.92) * mm});
            skLineSegment(sketch, "E430", {"start": v(-16.67, 3.92) * mm, "end": v(-16.73, 3.9) * mm});
            skLineSegment(sketch, "E431", {"start": v(-16.73, 3.9) * mm, "end": v(-16.78, 3.87) * mm});
            skLineSegment(sketch, "E432", {"start": v(-16.78, 3.87) * mm, "end": v(-16.82, 3.84) * mm});
            skLineSegment(sketch, "E433", {"start": v(-16.82, 3.84) * mm, "end": v(-16.86, 3.8) * mm});
            skLineSegment(sketch, "E434", {"start": v(-16.86, 3.8) * mm, "end": v(-16.9, 3.77) * mm});
            skLineSegment(sketch, "E435", {"start": v(-16.9, 3.77) * mm, "end": v(-16.92, 3.74) * mm});
            skLineSegment(sketch, "E436", {"start": v(-16.92, 3.74) * mm, "end": v(-16.95, 3.7) * mm});
            skLineSegment(sketch, "E437", {"start": v(-16.95, 3.7) * mm, "end": v(-16.98, 3.64) * mm});
            skLineSegment(sketch, "E438", {"start": v(-16.98, 3.64) * mm, "end": v(-17, 3.59) * mm});
            skLineSegment(sketch, "E439", {"start": v(-17, 3.59) * mm, "end": v(-17.03, 3.53) * mm});
            skLineSegment(sketch, "E440", {"start": v(-17.03, 3.53) * mm, "end": v(-17.06, 3.46) * mm});
            skLineSegment(sketch, "E441", {"start": v(-17.06, 3.46) * mm, "end": v(-17.08, 3.38) * mm});
            skLineSegment(sketch, "E442", {"start": v(-17.08, 3.38) * mm, "end": v(-17.1, 3.3) * mm});
            skLineSegment(sketch, "E443", {"start": v(-17.1, 3.3) * mm, "end": v(-17.13, 3.19) * mm});
            skLineSegment(sketch, "E444", {"start": v(-17.13, 3.19) * mm, "end": v(-17.15, 3.06) * mm});
            skLineSegment(sketch, "E445", {"start": v(-17.15, 3.06) * mm, "end": v(-17.17, 2.9) * mm});
            skLineSegment(sketch, "E446", {"start": v(-17.17, 2.9) * mm, "end": v(-17.2, 2.72) * mm});
            skLineSegment(sketch, "E447", {"start": v(-17.2, 2.72) * mm, "end": v(-17.22, 2.5) * mm});
            skLineSegment(sketch, "E448", {"start": v(-17.22, 2.5) * mm, "end": v(-17.24, 2.24) * mm});
            skLineSegment(sketch, "E449", {"start": v(-17.24, 2.24) * mm, "end": v(-17.26, 1.94) * mm});
            skLineSegment(sketch, "E450", {"start": v(-17.26, 1.94) * mm, "end": v(-17.28, 1.59) * mm});
            skLineSegment(sketch, "E451", {"start": v(-17.28, 1.59) * mm, "end": v(-17.3, 1.2) * mm});
            skLineSegment(sketch, "E452", {"start": v(-17.3, 1.2) * mm, "end": v(-17.32, 0.77) * mm});
            skLineSegment(sketch, "E453", {"start": v(-17.32, 0.77) * mm, "end": v(-17.34, 0.3) * mm});
            skLineSegment(sketch, "E454", {"start": v(-17.34, 0.3) * mm, "end": v(-17.36, -0.2) * mm});
            skLineSegment(sketch, "E455", {"start": v(-17.36, -0.2) * mm, "end": v(-17.37, -0.75) * mm});
            skLineSegment(sketch, "E456", {"start": v(-17.37, -0.75) * mm, "end": v(-17.37, -1.33) * mm});
            skLineSegment(sketch, "E457", {"start": v(-17.37, -1.33) * mm, "end": v(-17.38, -1.94) * mm});
            skLineSegment(sketch, "E458", {"start": v(-17.38, -1.94) * mm, "end": v(-17.38, -2.56) * mm});
            skLineSegment(sketch, "E459", {"start": v(-17.38, -2.56) * mm, "end": v(-17.38, -3.2) * mm});
            skLineSegment(sketch, "E460", {"start": v(-17.38, -3.2) * mm, "end": v(-17.37, -3.82) * mm});
            skLineSegment(sketch, "E461", {"start": v(-17.37, -3.82) * mm, "end": v(-17.37, -4.4) * mm});
            skLineSegment(sketch, "E462", {"start": v(-17.37, -4.4) * mm, "end": v(-17.37, -4.96) * mm});
            skLineSegment(sketch, "E463", {"start": v(-17.37, -4.96) * mm, "end": v(-17.37, -5.45) * mm});
            skLineSegment(sketch, "E464", {"start": v(-17.37, -5.45) * mm, "end": v(-17.37, -5.91) * mm});
            skLineSegment(sketch, "E465", {"start": v(-17.37, -5.91) * mm, "end": v(-16.5, -5.91) * mm});
            skArc(sketch, "E466", {"start": v(-16.5, -15.31) * mm, "mid": v(-16.37, -15.63) * mm, "end": v(-16.06, -15.76) * mm});
            skLineSegment(sketch, "E467", {"start": v(-15.95, -15.76) * mm, "end": v(-16.06, -15.76) * mm});
            skLineSegment(sketch, "E468", {"start": v(-15.95, 3.3) * mm, "end": v(-16.06, 3.3) * mm});
            skArc(sketch, "E469", {"start": v(-16.06, 3.3) * mm, "mid": v(-16.37, 3.16) * mm, "end": v(-16.5, 2.85) * mm});
            skLineSegment(sketch, "E470", {"start": v(-16.5, -5.91) * mm, "end": v(-16.5, 2.85) * mm});
            skLineSegment(sketch, "E471", {"start": v(-15.95, 9) * mm, "end": v(-15.35, 9.03) * mm});
            skLineSegment(sketch, "E472", {"start": v(-15.35, 9.03) * mm, "end": v(-14.81, 9.08) * mm});
            skLineSegment(sketch, "E473", {"start": v(-14.81, 9.08) * mm, "end": v(-14.32, 9.14) * mm});
            skLineSegment(sketch, "E474", {"start": v(-14.32, 9.14) * mm, "end": v(-13.87, 9.21) * mm});
            skLineSegment(sketch, "E475", {"start": v(-13.87, 9.21) * mm, "end": v(-13.46, 9.3) * mm});
            skLineSegment(sketch, "E476", {"start": v(-13.46, 9.3) * mm, "end": v(-13.1, 9.39) * mm});
            skLineSegment(sketch, "E477", {"start": v(-13.1, 9.39) * mm, "end": v(-12.76, 9.48) * mm});
            skLineSegment(sketch, "E478", {"start": v(-12.76, 9.48) * mm, "end": v(-12.45, 9.57) * mm});
            skLineSegment(sketch, "E479", {"start": v(-12.45, 9.57) * mm, "end": v(-12.17, 9.67) * mm});
            skLineSegment(sketch, "E480", {"start": v(-12.17, 9.67) * mm, "end": v(-11.92, 9.76) * mm});
            skLineSegment(sketch, "E481", {"start": v(-11.92, 9.76) * mm, "end": v(-11.69, 9.85) * mm});
            skLineSegment(sketch, "E482", {"start": v(-11.69, 9.85) * mm, "end": v(-11.48, 9.93) * mm});
            skLineSegment(sketch, "E483", {"start": v(-11.48, 9.93) * mm, "end": v(-11.29, 10.01) * mm});
            skLineSegment(sketch, "E484", {"start": v(-11.29, 10.01) * mm, "end": v(-11.11, 10.09) * mm});
            skLineSegment(sketch, "E485", {"start": v(-11.11, 10.09) * mm, "end": v(-10.96, 10.15) * mm});
            skLineSegment(sketch, "E486", {"start": v(-10.96, 10.15) * mm, "end": v(-10.82, 10.22) * mm});
            skLineSegment(sketch, "E487", {"start": v(-10.82, 10.22) * mm, "end": v(-10.7, 10.27) * mm});
            skLineSegment(sketch, "E488", {"start": v(-10.7, 10.27) * mm, "end": v(-10.58, 10.32) * mm});
            skLineSegment(sketch, "E489", {"start": v(-10.58, 10.32) * mm, "end": v(-10.47, 10.35) * mm});
            skLineSegment(sketch, "E490", {"start": v(-10.47, 10.35) * mm, "end": v(-10.38, 10.39) * mm});
            skLineSegment(sketch, "E491", {"start": v(-10.38, 10.39) * mm, "end": v(-10.3, 10.42) * mm});
            skLineSegment(sketch, "E492", {"start": v(-10.3, 10.42) * mm, "end": v(-10.2, 10.44) * mm});
            skLineSegment(sketch, "E493", {"start": v(-10.2, 10.44) * mm, "end": v(-10.13, 10.46) * mm});
            skLineSegment(sketch, "E494", {"start": v(-10.13, 10.46) * mm, "end": v(-10.05, 10.47) * mm});
            skLineSegment(sketch, "E495", {"start": v(-10.05, 10.47) * mm, "end": v(-9.98, 10.48) * mm});
            skLineSegment(sketch, "E496", {"start": v(-9.98, 10.48) * mm, "end": v(-9.9, 10.5) * mm});
            skLineSegment(sketch, "E497", {"start": v(-9.9, 10.5) * mm, "end": v(-9.82, 10.5) * mm});
            skLineSegment(sketch, "E498", {"start": v(-9.82, 10.5) * mm, "end": v(-9.75, 10.5) * mm});
            skLineSegment(sketch, "E499", {"start": v(-9.75, 10.5) * mm, "end": v(-9.67, 10.5) * mm});
            skLineSegment(sketch, "E500", {"start": v(-9.67, 10.5) * mm, "end": v(-9.6, 10.5) * mm});
            skLineSegment(sketch, "E501", {"start": v(-9.6, 10.5) * mm, "end": v(-9.52, 10.48) * mm});
            skLineSegment(sketch, "E502", {"start": v(-9.52, 10.48) * mm, "end": v(-9.44, 10.47) * mm});
            skLineSegment(sketch, "E503", {"start": v(-9.44, 10.47) * mm, "end": v(-9.36, 10.46) * mm});
            skLineSegment(sketch, "E504", {"start": v(-9.36, 10.46) * mm, "end": v(-9.28, 10.44) * mm});
            skLineSegment(sketch, "E505", {"start": v(-9.28, 10.44) * mm, "end": v(-9.2, 10.41) * mm});
            skLineSegment(sketch, "E506", {"start": v(-9.2, 10.41) * mm, "end": v(-9.1, 10.39) * mm});
            skLineSegment(sketch, "E507", {"start": v(-9.1, 10.39) * mm, "end": v(-9.02, 10.36) * mm});
            skLineSegment(sketch, "E508", {"start": v(-9.02, 10.36) * mm, "end": v(-8.94, 10.32) * mm});
            skLineSegment(sketch, "E509", {"start": v(-8.94, 10.32) * mm, "end": v(-8.85, 10.28) * mm});
            skLineSegment(sketch, "E510", {"start": v(-8.85, 10.28) * mm, "end": v(-8.76, 10.24) * mm});
            skLineSegment(sketch, "E511", {"start": v(-8.76, 10.24) * mm, "end": v(-8.68, 10.2) * mm});
            skLineSegment(sketch, "E512", {"start": v(-8.68, 10.2) * mm, "end": v(-8.59, 10.14) * mm});
            skLineSegment(sketch, "E513", {"start": v(-8.59, 10.14) * mm, "end": v(-8.5, 10.09) * mm});
            skLineSegment(sketch, "E514", {"start": v(-8.5, 10.09) * mm, "end": v(-8.42, 10.03) * mm});
            skLineSegment(sketch, "E515", {"start": v(-8.42, 10.03) * mm, "end": v(-8.33, 9.97) * mm});
            skLineSegment(sketch, "E516", {"start": v(-8.33, 9.97) * mm, "end": v(-8.25, 9.9) * mm});
            skLineSegment(sketch, "E517", {"start": v(-8.25, 9.9) * mm, "end": v(-8.17, 9.83) * mm});
            skLineSegment(sketch, "E518", {"start": v(-8.17, 9.83) * mm, "end": v(-8.09, 9.76) * mm});
            skLineSegment(sketch, "E519", {"start": v(-8.09, 9.76) * mm, "end": v(-8, 9.7) * mm});
            skLineSegment(sketch, "E520", {"start": v(-8, 9.7) * mm, "end": v(-7.93, 9.62) * mm});
            skLineSegment(sketch, "E521", {"start": v(-7.93, 9.62) * mm, "end": v(-7.85, 9.54) * mm});
            skLineSegment(sketch, "E522", {"start": v(-7.85, 9.54) * mm, "end": v(-7.77, 9.45) * mm});
            skLineSegment(sketch, "E523", {"start": v(-7.77, 9.45) * mm, "end": v(-7.7, 9.36) * mm});
            skLineSegment(sketch, "E524", {"start": v(-7.7, 9.36) * mm, "end": v(-7.62, 9.27) * mm});
            skLineSegment(sketch, "E525", {"start": v(-7.62, 9.27) * mm, "end": v(-7.54, 9.17) * mm});
            skLineSegment(sketch, "E526", {"start": v(-7.54, 9.17) * mm, "end": v(-7.46, 9.06) * mm});
            skLineSegment(sketch, "E527", {"start": v(-7.46, 9.06) * mm, "end": v(-7.37, 8.94) * mm});
            skLineSegment(sketch, "E528", {"start": v(-7.37, 8.94) * mm, "end": v(-7.3, 8.82) * mm});
            skLineSegment(sketch, "E529", {"start": v(-7.3, 8.82) * mm, "end": v(-7.2, 8.7) * mm});
            skLineSegment(sketch, "E530", {"start": v(-7.2, 8.7) * mm, "end": v(-7.13, 8.57) * mm});
            skLineSegment(sketch, "E531", {"start": v(-7.13, 8.57) * mm, "end": v(-7.06, 8.45) * mm});
            skLineSegment(sketch, "E532", {"start": v(-7.06, 8.45) * mm, "end": v(-7, 8.33) * mm});
            skLineSegment(sketch, "E533", {"start": v(-7, 8.33) * mm, "end": v(-6.94, 8.22) * mm});
            skLineSegment(sketch, "E534", {"start": v(-6.94, 8.22) * mm, "end": v(-6.89, 8.11) * mm});
            skLineSegment(sketch, "E535", {"start": v(-6.89, 8.11) * mm, "end": v(-6.85, 8.02) * mm});
            skLineSegment(sketch, "E536", {"start": v(-6.85, 8.02) * mm, "end": v(-6.82, 7.94) * mm});
            skLineSegment(sketch, "E537", {"start": v(-6.82, 7.94) * mm, "end": v(-6.8, 7.87) * mm});
            skLineSegment(sketch, "E538", {"start": v(-6.8, 7.87) * mm, "end": v(-6.8, 7.8) * mm});
            skLineSegment(sketch, "E539", {"start": v(-6.8, 7.8) * mm, "end": v(-6.8, 7.74) * mm});
            skLineSegment(sketch, "E540", {"start": v(-6.8, 7.74) * mm, "end": v(-6.8, 7.7) * mm});
            skLineSegment(sketch, "E541", {"start": v(-6.8, 7.7) * mm, "end": v(-6.82, 7.64) * mm});
            skLineSegment(sketch, "E542", {"start": v(-6.82, 7.64) * mm, "end": v(-6.84, 7.6) * mm});
            skLineSegment(sketch, "E543", {"start": v(-6.84, 7.6) * mm, "end": v(-6.87, 7.55) * mm});
            skLineSegment(sketch, "E544", {"start": v(-6.87, 7.55) * mm, "end": v(-6.9, 7.5) * mm});
            skLineSegment(sketch, "E545", {"start": v(-6.9, 7.5) * mm, "end": v(-6.92, 7.47) * mm});
            skLineSegment(sketch, "E546", {"start": v(-6.92, 7.47) * mm, "end": v(-6.96, 7.43) * mm});
            skLineSegment(sketch, "E547", {"start": v(-6.96, 7.43) * mm, "end": v(-7, 7.4) * mm});
            skLineSegment(sketch, "E548", {"start": v(-7, 7.4) * mm, "end": v(-7.04, 7.36) * mm});
            skLineSegment(sketch, "E549", {"start": v(-7.04, 7.36) * mm, "end": v(-7.08, 7.34) * mm});
            skLineSegment(sketch, "E550", {"start": v(-7.08, 7.34) * mm, "end": v(-7.12, 7.31) * mm});
            skLineSegment(sketch, "E551", {"start": v(-7.12, 7.31) * mm, "end": v(-7.17, 7.3) * mm});
            skLineSegment(sketch, "E552", {"start": v(-7.17, 7.3) * mm, "end": v(-7.22, 7.28) * mm});
            skLineSegment(sketch, "E553", {"start": v(-7.22, 7.28) * mm, "end": v(-7.27, 7.27) * mm});
            skLineSegment(sketch, "E554", {"start": v(-7.27, 7.27) * mm, "end": v(-7.31, 7.26) * mm});
            skLineSegment(sketch, "E555", {"start": v(-7.31, 7.26) * mm, "end": v(-7.36, 7.26) * mm});
            skLineSegment(sketch, "E556", {"start": v(-7.36, 7.26) * mm, "end": v(-7.41, 7.26) * mm});
            skLineSegment(sketch, "E557", {"start": v(-7.41, 7.26) * mm, "end": v(-7.46, 7.26) * mm});
            skLineSegment(sketch, "E558", {"start": v(-7.46, 7.26) * mm, "end": v(-7.5, 7.27) * mm});
            skLineSegment(sketch, "E559", {"start": v(-7.5, 7.27) * mm, "end": v(-7.55, 7.28) * mm});
            skLineSegment(sketch, "E560", {"start": v(-7.55, 7.28) * mm, "end": v(-7.6, 7.3) * mm});
            skLineSegment(sketch, "E561", {"start": v(-7.6, 7.3) * mm, "end": v(-7.64, 7.3) * mm});
            skLineSegment(sketch, "E562", {"start": v(-7.64, 7.3) * mm, "end": v(-7.68, 7.33) * mm});
            skLineSegment(sketch, "E563", {"start": v(-7.68, 7.33) * mm, "end": v(-7.72, 7.36) * mm});
            skLineSegment(sketch, "E564", {"start": v(-7.72, 7.36) * mm, "end": v(-7.76, 7.4) * mm});
            skLineSegment(sketch, "E565", {"start": v(-7.76, 7.4) * mm, "end": v(-7.8, 7.43) * mm});
            skLineSegment(sketch, "E566", {"start": v(-7.8, 7.43) * mm, "end": v(-7.84, 7.48) * mm});
            skLineSegment(sketch, "E567", {"start": v(-7.84, 7.48) * mm, "end": v(-7.88, 7.53) * mm});
            skLineSegment(sketch, "E568", {"start": v(-7.88, 7.53) * mm, "end": v(-7.93, 7.59) * mm});
            skLineSegment(sketch, "E569", {"start": v(-7.93, 7.59) * mm, "end": v(-7.97, 7.65) * mm});
            skLineSegment(sketch, "E570", {"start": v(-7.97, 7.65) * mm, "end": v(-8.02, 7.72) * mm});
            skLineSegment(sketch, "E571", {"start": v(-8.02, 7.72) * mm, "end": v(-8.07, 7.8) * mm});
            skLineSegment(sketch, "E572", {"start": v(-8.07, 7.8) * mm, "end": v(-8.12, 7.87) * mm});
            skLineSegment(sketch, "E573", {"start": v(-8.12, 7.87) * mm, "end": v(-8.18, 7.96) * mm});
            skLineSegment(sketch, "E574", {"start": v(-8.18, 7.96) * mm, "end": v(-8.24, 8.04) * mm});
            skLineSegment(sketch, "E575", {"start": v(-8.24, 8.04) * mm, "end": v(-8.3, 8.13) * mm});
            skLineSegment(sketch, "E576", {"start": v(-8.3, 8.13) * mm, "end": v(-8.37, 8.23) * mm});
            skLineSegment(sketch, "E577", {"start": v(-8.37, 8.23) * mm, "end": v(-8.44, 8.32) * mm});
            skLineSegment(sketch, "E578", {"start": v(-8.44, 8.32) * mm, "end": v(-8.5, 8.41) * mm});
            skLineSegment(sketch, "E579", {"start": v(-8.5, 8.41) * mm, "end": v(-8.58, 8.5) * mm});
            skLineSegment(sketch, "E580", {"start": v(-8.58, 8.5) * mm, "end": v(-8.66, 8.6) * mm});
            skLineSegment(sketch, "E581", {"start": v(-8.66, 8.6) * mm, "end": v(-8.73, 8.68) * mm});
            skLineSegment(sketch, "E582", {"start": v(-8.73, 8.68) * mm, "end": v(-8.81, 8.76) * mm});
            skLineSegment(sketch, "E583", {"start": v(-8.81, 8.76) * mm, "end": v(-8.89, 8.83) * mm});
            skLineSegment(sketch, "E584", {"start": v(-8.89, 8.83) * mm, "end": v(-8.97, 8.9) * mm});
            skLineSegment(sketch, "E585", {"start": v(-8.97, 8.9) * mm, "end": v(-9.04, 8.97) * mm});
            skLineSegment(sketch, "E586", {"start": v(-9.04, 8.97) * mm, "end": v(-9.12, 9.02) * mm});
            skLineSegment(sketch, "E587", {"start": v(-9.12, 9.02) * mm, "end": v(-9.2, 9.08) * mm});
            skLineSegment(sketch, "E588", {"start": v(-9.2, 9.08) * mm, "end": v(-9.26, 9.12) * mm});
            skLineSegment(sketch, "E589", {"start": v(-9.26, 9.12) * mm, "end": v(-9.33, 9.16) * mm});
            skLineSegment(sketch, "E590", {"start": v(-9.33, 9.16) * mm, "end": v(-9.4, 9.2) * mm});
            skLineSegment(sketch, "E591", {"start": v(-9.4, 9.2) * mm, "end": v(-9.47, 9.22) * mm});
            skLineSegment(sketch, "E592", {"start": v(-9.47, 9.22) * mm, "end": v(-9.53, 9.24) * mm});
            skLineSegment(sketch, "E593", {"start": v(-9.53, 9.24) * mm, "end": v(-9.59, 9.25) * mm});
            skLineSegment(sketch, "E594", {"start": v(-9.59, 9.25) * mm, "end": v(-9.65, 9.26) * mm});
            skLineSegment(sketch, "E595", {"start": v(-9.65, 9.26) * mm, "end": v(-9.7, 9.27) * mm});
            skLineSegment(sketch, "E596", {"start": v(-9.7, 9.27) * mm, "end": v(-9.76, 9.27) * mm});
            skLineSegment(sketch, "E597", {"start": v(-9.76, 9.27) * mm, "end": v(-9.82, 9.26) * mm});
            skLineSegment(sketch, "E598", {"start": v(-9.82, 9.26) * mm, "end": v(-9.87, 9.26) * mm});
            skLineSegment(sketch, "E599", {"start": v(-9.87, 9.26) * mm, "end": v(-9.93, 9.25) * mm});
            skLineSegment(sketch, "E600", {"start": v(-9.93, 9.25) * mm, "end": v(-9.99, 9.24) * mm});
            skLineSegment(sketch, "E601", {"start": v(-9.99, 9.24) * mm, "end": v(-10.05, 9.22) * mm});
            skLineSegment(sketch, "E602", {"start": v(-10.05, 9.22) * mm, "end": v(-10.11, 9.2) * mm});
            skLineSegment(sketch, "E603", {"start": v(-10.11, 9.2) * mm, "end": v(-10.18, 9.18) * mm});
            skLineSegment(sketch, "E604", {"start": v(-10.18, 9.18) * mm, "end": v(-10.26, 9.15) * mm});
            skLineSegment(sketch, "E605", {"start": v(-10.26, 9.15) * mm, "end": v(-10.34, 9.12) * mm});
            skLineSegment(sketch, "E606", {"start": v(-10.34, 9.12) * mm, "end": v(-10.43, 9.08) * mm});
            skLineSegment(sketch, "E607", {"start": v(-10.43, 9.08) * mm, "end": v(-10.54, 9.03) * mm});
            skLineSegment(sketch, "E608", {"start": v(-10.54, 9.03) * mm, "end": v(-10.65, 8.98) * mm});
            skLineSegment(sketch, "E609", {"start": v(-10.65, 8.98) * mm, "end": v(-10.76, 8.93) * mm});
            skLineSegment(sketch, "E610", {"start": v(-10.76, 8.93) * mm, "end": v(-10.89, 8.87) * mm});
            skLineSegment(sketch, "E611", {"start": v(-10.89, 8.87) * mm, "end": v(-11.02, 8.8) * mm});
            skLineSegment(sketch, "E612", {"start": v(-11.02, 8.8) * mm, "end": v(-11.15, 8.75) * mm});
            skLineSegment(sketch, "E613", {"start": v(-11.15, 8.75) * mm, "end": v(-11.29, 8.68) * mm});
            skLineSegment(sketch, "E614", {"start": v(-11.29, 8.68) * mm, "end": v(-11.42, 8.62) * mm});
            skLineSegment(sketch, "E615", {"start": v(-11.42, 8.62) * mm, "end": v(-11.56, 8.56) * mm});
            skLineSegment(sketch, "E616", {"start": v(-11.56, 8.56) * mm, "end": v(-11.7, 8.5) * mm});
            skLineSegment(sketch, "E617", {"start": v(-11.7, 8.5) * mm, "end": v(-11.84, 8.45) * mm});
            skLineSegment(sketch, "E618", {"start": v(-11.84, 8.45) * mm, "end": v(-11.98, 8.4) * mm});
            skLineSegment(sketch, "E619", {"start": v(-11.98, 8.4) * mm, "end": v(-12.12, 8.34) * mm});
            skLineSegment(sketch, "E620", {"start": v(-12.12, 8.34) * mm, "end": v(-12.27, 8.29) * mm});
            skLineSegment(sketch, "E621", {"start": v(-12.27, 8.29) * mm, "end": v(-12.41, 8.24) * mm});
            skLineSegment(sketch, "E622", {"start": v(-12.41, 8.24) * mm, "end": v(-12.56, 8.2) * mm});
            skLineSegment(sketch, "E623", {"start": v(-12.56, 8.2) * mm, "end": v(-12.7, 8.15) * mm});
            skLineSegment(sketch, "E624", {"start": v(-12.7, 8.15) * mm, "end": v(-12.86, 8.11) * mm});
            skLineSegment(sketch, "E625", {"start": v(-12.86, 8.11) * mm, "end": v(-13.01, 8.07) * mm});
            skLineSegment(sketch, "E626", {"start": v(-13.01, 8.07) * mm, "end": v(-13.17, 8.04) * mm});
            skLineSegment(sketch, "E627", {"start": v(-13.17, 8.04) * mm, "end": v(-13.34, 8) * mm});
            skLineSegment(sketch, "E628", {"start": v(-13.34, 8) * mm, "end": v(-13.52, 7.98) * mm});
            skLineSegment(sketch, "E629", {"start": v(-13.52, 7.98) * mm, "end": v(-13.7, 7.95) * mm});
            skLineSegment(sketch, "E630", {"start": v(-13.7, 7.95) * mm, "end": v(-13.9, 7.92) * mm});
            skLineSegment(sketch, "E631", {"start": v(-13.9, 7.92) * mm, "end": v(-14.11, 7.9) * mm});
            skLineSegment(sketch, "E632", {"start": v(-14.11, 7.9) * mm, "end": v(-14.32, 7.87) * mm});
            skLineSegment(sketch, "E633", {"start": v(-14.32, 7.87) * mm, "end": v(-14.54, 7.85) * mm});
            skLineSegment(sketch, "E634", {"start": v(-14.54, 7.85) * mm, "end": v(-14.75, 7.83) * mm});
            skLineSegment(sketch, "E635", {"start": v(-14.75, 7.83) * mm, "end": v(-14.94, 7.8) * mm});
            skLineSegment(sketch, "E636", {"start": v(-14.94, 7.8) * mm, "end": v(-15.12, 7.8) * mm});
            skLineSegment(sketch, "E637", {"start": v(-15.12, 7.8) * mm, "end": v(-15.27, 7.79) * mm});
            skLineSegment(sketch, "E638", {"start": v(-15.27, 7.79) * mm, "end": v(-15.4, 7.79) * mm});
            skLineSegment(sketch, "E639", {"start": v(-15.4, 7.79) * mm, "end": v(-14.3, 9.06) * mm});
            skLineSegment(sketch, "E640", {"start": v(-14.3, 9.06) * mm, "end": v(-12.17, 9.59) * mm});
            skLineSegment(sketch, "E641", {"start": v(-12.17, 9.59) * mm, "end": v(-10.67, 10.3) * mm});
            skLineSegment(sketch, "E642", {"start": v(-10.67, 10.3) * mm, "end": v(-10.04, 10.5) * mm});
            skLineSegment(sketch, "E643", {"start": v(-10.04, 10.5) * mm, "end": v(-9.46, 10.5) * mm});
            skLineSegment(sketch, "E644", {"start": v(-9.46, 10.5) * mm, "end": v(-8.76, 10.29) * mm});
            skLineSegment(sketch, "E645", {"start": v(-8.76, 10.29) * mm, "end": v(-8.07, 9.79) * mm});
            skLineSegment(sketch, "E646", {"start": v(-8.07, 9.79) * mm, "end": v(-7.47, 9.14) * mm});
            skLineSegment(sketch, "E647", {"start": v(-7.47, 9.14) * mm, "end": v(-6.76, 7.99) * mm});
            skLineSegment(sketch, "E648", {"start": v(-6.76, 7.99) * mm, "end": v(-6.8, 7.58) * mm});
            skLineSegment(sketch, "E649", {"start": v(-6.8, 7.58) * mm, "end": v(-7.1, 7.26) * mm});
            skLineSegment(sketch, "E650", {"start": v(-7.1, 7.26) * mm, "end": v(-7.52, 7.23) * mm});
            skLineSegment(sketch, "E651", {"start": v(-7.52, 7.23) * mm, "end": v(-7.83, 7.4) * mm});
            skLineSegment(sketch, "E652", {"start": v(-7.83, 7.4) * mm, "end": v(-8.2, 8.01) * mm});
            skLineSegment(sketch, "E653", {"start": v(-8.2, 8.01) * mm, "end": v(-8.8, 8.82) * mm});
            skLineSegment(sketch, "E654", {"start": v(-8.8, 8.82) * mm, "end": v(-9.43, 9.26) * mm});
            skLineSegment(sketch, "E655", {"start": v(-9.43, 9.26) * mm, "end": v(-9.87, 9.29) * mm});
            skLineSegment(sketch, "E656", {"start": v(-9.87, 9.29) * mm, "end": v(-10.33, 9.14) * mm});
            skLineSegment(sketch, "E657", {"start": v(-10.33, 9.14) * mm, "end": v(-11.42, 8.6) * mm});
            skLineSegment(sketch, "E658", {"start": v(-11.42, 8.6) * mm, "end": v(-12.54, 8.16) * mm});
            skLineSegment(sketch, "E659", {"start": v(-12.54, 8.16) * mm, "end": v(-13.77, 7.9) * mm});
            skLineSegment(sketch, "E660", {"start": v(-13.77, 7.9) * mm, "end": v(-15.12, 7.79) * mm});
            skLineSegment(sketch, "E661", {"start": v(-15.12, 7.79) * mm, "end": v(-15.4, 7.79) * mm});
            skArc(sketch, "E662", {"start": v(-15.85, -15.76) * mm, "mid": v(-15.53, -15.63) * mm, "end": v(-15.4, -15.31) * mm});
            skArc(sketch, "E663", {"start": v(-15.4, 2.85) * mm, "mid": v(-15.53, 3.16) * mm, "end": v(-15.85, 3.3) * mm});
            skLineSegment(sketch, "E664", {"start": v(-15.4, -15.31) * mm, "end": v(-15.4, -6.33) * mm});
            skLineSegment(sketch, "E665", {"start": v(-15.4, -6.33) * mm, "end": v(-14.52, -6.33) * mm});
            skLineSegment(sketch, "E666", {"start": v(-14.52, -6.33) * mm, "end": v(-14.5, -6.48) * mm});
            skLineSegment(sketch, "E667", {"start": v(-14.5, -6.48) * mm, "end": v(-14.5, -6.68) * mm});
            skLineSegment(sketch, "E668", {"start": v(-14.5, -6.68) * mm, "end": v(-14.47, -6.82) * mm});
            skLineSegment(sketch, "E669", {"start": v(-14.47, -6.82) * mm, "end": v(-14.45, -6.92) * mm});
            skLineSegment(sketch, "E670", {"start": v(-14.45, -6.92) * mm, "end": v(-14.43, -6.98) * mm});
            skLineSegment(sketch, "E671", {"start": v(-14.43, -6.98) * mm, "end": v(-14.4, -7.02) * mm});
            skLineSegment(sketch, "E672", {"start": v(-14.4, -7.02) * mm, "end": v(-14.37, -7.04) * mm});
            skLineSegment(sketch, "E673", {"start": v(-14.37, -7.04) * mm, "end": v(-14.33, -7.06) * mm});
            skLineSegment(sketch, "E674", {"start": v(-14.33, -7.06) * mm, "end": v(-14.3, -7.08) * mm});
            skLineSegment(sketch, "E675", {"start": v(-14.3, -7.08) * mm, "end": v(-14.26, -7.1) * mm});
            skLineSegment(sketch, "E676", {"start": v(-14.26, -7.1) * mm, "end": v(-14.22, -7.11) * mm});
            skLineSegment(sketch, "E677", {"start": v(-14.22, -7.11) * mm, "end": v(-14.18, -7.12) * mm});
            skLineSegment(sketch, "E678", {"start": v(-14.18, -7.12) * mm, "end": v(-14.14, -7.13) * mm});
            skLineSegment(sketch, "E679", {"start": v(-14.14, -7.13) * mm, "end": v(-14.1, -7.13) * mm});
            skLineSegment(sketch, "E680", {"start": v(-14.1, -7.13) * mm, "end": v(-14.06, -7.13) * mm});
            skLineSegment(sketch, "E681", {"start": v(-14.06, -7.13) * mm, "end": v(-14.01, -7.13) * mm});
            skLineSegment(sketch, "E682", {"start": v(-14.01, -7.13) * mm, "end": v(-13.97, -7.12) * mm});
            skLineSegment(sketch, "E683", {"start": v(-13.97, -7.12) * mm, "end": v(-13.93, -7.11) * mm});
            skLineSegment(sketch, "E684", {"start": v(-13.93, -7.11) * mm, "end": v(-13.89, -7.1) * mm});
            skLineSegment(sketch, "E685", {"start": v(-13.89, -7.1) * mm, "end": v(-13.85, -7.09) * mm});
            skLineSegment(sketch, "E686", {"start": v(-13.85, -7.09) * mm, "end": v(-13.81, -7.07) * mm});
            skLineSegment(sketch, "E687", {"start": v(-13.81, -7.07) * mm, "end": v(-13.78, -7.05) * mm});
            skLineSegment(sketch, "E688", {"start": v(-13.78, -7.05) * mm, "end": v(-13.74, -7.03) * mm});
            skLineSegment(sketch, "E689", {"start": v(-13.74, -7.03) * mm, "end": v(-13.71, -7) * mm});
            skLineSegment(sketch, "E690", {"start": v(-13.71, -7) * mm, "end": v(-13.69, -6.97) * mm});
            skLineSegment(sketch, "E691", {"start": v(-13.69, -6.97) * mm, "end": v(-13.67, -6.91) * mm});
            skLineSegment(sketch, "E692", {"start": v(-13.67, -6.91) * mm, "end": v(-13.64, -6.83) * mm});
            skLineSegment(sketch, "E693", {"start": v(-13.64, -6.83) * mm, "end": v(-13.63, -6.72) * mm});
            skLineSegment(sketch, "E694", {"start": v(-13.63, -6.72) * mm, "end": v(-13.61, -6.57) * mm});
            skLineSegment(sketch, "E695", {"start": v(-13.61, -6.57) * mm, "end": v(-13.6, -6.37) * mm});
            skLineSegment(sketch, "E696", {"start": v(-13.6, -6.37) * mm, "end": v(-13.6, -6.1) * mm});
            skLineSegment(sketch, "E697", {"start": v(-13.6, -6.1) * mm, "end": v(-13.58, -5.8) * mm});
            skLineSegment(sketch, "E698", {"start": v(-13.58, -5.8) * mm, "end": v(-13.58, -5.42) * mm});
            skLineSegment(sketch, "E699", {"start": v(-13.58, -5.42) * mm, "end": v(-13.58, -5) * mm});
            skLineSegment(sketch, "E700", {"start": v(-13.58, -5) * mm, "end": v(-13.58, -4.53) * mm});
            skLineSegment(sketch, "E701", {"start": v(-13.58, -4.53) * mm, "end": v(-13.58, -4.03) * mm});
            skLineSegment(sketch, "E702", {"start": v(-13.58, -4.03) * mm, "end": v(-13.58, -3.5) * mm});
            skLineSegment(sketch, "E703", {"start": v(-13.58, -3.5) * mm, "end": v(-13.59, -2.96) * mm});
            skLineSegment(sketch, "E704", {"start": v(-13.59, -2.96) * mm, "end": v(-13.6, -2.4) * mm});
            skLineSegment(sketch, "E705", {"start": v(-13.6, -2.4) * mm, "end": v(-13.6, -1.84) * mm});
            skLineSegment(sketch, "E706", {"start": v(-13.6, -1.84) * mm, "end": v(-13.62, -1.28) * mm});
            skLineSegment(sketch, "E707", {"start": v(-13.62, -1.28) * mm, "end": v(-13.63, -0.72) * mm});
            skLineSegment(sketch, "E708", {"start": v(-13.63, -0.72) * mm, "end": v(-13.65, -0.18) * mm});
            skLineSegment(sketch, "E709", {"start": v(-13.65, -0.18) * mm, "end": v(-13.67, 0.34) * mm});
            skLineSegment(sketch, "E710", {"start": v(-13.67, 0.34) * mm, "end": v(-13.69, 0.83) * mm});
            skLineSegment(sketch, "E711", {"start": v(-13.69, 0.83) * mm, "end": v(-13.71, 1.3) * mm});
            skLineSegment(sketch, "E712", {"start": v(-13.71, 1.3) * mm, "end": v(-13.74, 1.72) * mm});
            skLineSegment(sketch, "E713", {"start": v(-13.74, 1.72) * mm, "end": v(-13.77, 2.1) * mm});
            skLineSegment(sketch, "E714", {"start": v(-13.77, 2.1) * mm, "end": v(-13.8, 2.44) * mm});
            skLineSegment(sketch, "E715", {"start": v(-13.8, 2.44) * mm, "end": v(-13.85, 2.74) * mm});
            skLineSegment(sketch, "E716", {"start": v(-13.85, 2.74) * mm, "end": v(-13.89, 3) * mm});
            skLineSegment(sketch, "E717", {"start": v(-13.89, 3) * mm, "end": v(-13.93, 3.24) * mm});
            skLineSegment(sketch, "E718", {"start": v(-13.93, 3.24) * mm, "end": v(-13.98, 3.45) * mm});
            skLineSegment(sketch, "E719", {"start": v(-13.98, 3.45) * mm, "end": v(-14.04, 3.64) * mm});
            skLineSegment(sketch, "E720", {"start": v(-14.04, 3.64) * mm, "end": v(-14.1, 3.8) * mm});
            skLineSegment(sketch, "E721", {"start": v(-14.1, 3.8) * mm, "end": v(-14.16, 3.95) * mm});
            skLineSegment(sketch, "E722", {"start": v(-14.16, 3.95) * mm, "end": v(-14.22, 4.08) * mm});
            skLineSegment(sketch, "E723", {"start": v(-14.22, 4.08) * mm, "end": v(-14.29, 4.2) * mm});
            skLineSegment(sketch, "E724", {"start": v(-14.29, 4.2) * mm, "end": v(-14.36, 4.3) * mm});
            skLineSegment(sketch, "E725", {"start": v(-14.36, 4.3) * mm, "end": v(-14.43, 4.39) * mm});
            skLineSegment(sketch, "E726", {"start": v(-14.43, 4.39) * mm, "end": v(-14.5, 4.46) * mm});
            skLineSegment(sketch, "E727", {"start": v(-14.5, 4.46) * mm, "end": v(-14.59, 4.53) * mm});
            skLineSegment(sketch, "E728", {"start": v(-14.59, 4.53) * mm, "end": v(-14.67, 4.6) * mm});
            skLineSegment(sketch, "E729", {"start": v(-14.67, 4.6) * mm, "end": v(-14.75, 4.65) * mm});
            skLineSegment(sketch, "E730", {"start": v(-14.75, 4.65) * mm, "end": v(-14.83, 4.7) * mm});
            skLineSegment(sketch, "E731", {"start": v(-14.83, 4.7) * mm, "end": v(-14.92, 4.73) * mm});
            skLineSegment(sketch, "E732", {"start": v(-14.92, 4.73) * mm, "end": v(-15, 4.76) * mm});
            skLineSegment(sketch, "E733", {"start": v(-15, 4.76) * mm, "end": v(-15.1, 4.79) * mm});
            skLineSegment(sketch, "E734", {"start": v(-15.1, 4.79) * mm, "end": v(-15.2, 4.81) * mm});
            skLineSegment(sketch, "E735", {"start": v(-15.2, 4.81) * mm, "end": v(-15.4, 4.84) * mm});
            skLineSegment(sketch, "E736", {"start": v(-15.4, 4.84) * mm, "end": v(-15.4, 7.79) * mm});
            skLineSegment(sketch, "E737", {"start": v(-15.95, 3.98) * mm, "end": v(-15.74, 3.98) * mm});
            skLineSegment(sketch, "E738", {"start": v(-15.74, 3.98) * mm, "end": v(-15.56, 3.97) * mm});
            skLineSegment(sketch, "E739", {"start": v(-15.56, 3.97) * mm, "end": v(-15.42, 3.96) * mm});
            skLineSegment(sketch, "E740", {"start": v(-15.42, 3.96) * mm, "end": v(-15.32, 3.94) * mm});
            skLineSegment(sketch, "E741", {"start": v(-15.32, 3.94) * mm, "end": v(-15.23, 3.92) * mm});
            skLineSegment(sketch, "E742", {"start": v(-15.23, 3.92) * mm, "end": v(-15.17, 3.9) * mm});
            skLineSegment(sketch, "E743", {"start": v(-15.17, 3.9) * mm, "end": v(-15.12, 3.87) * mm});
            skLineSegment(sketch, "E744", {"start": v(-15.12, 3.87) * mm, "end": v(-15.08, 3.84) * mm});
            skLineSegment(sketch, "E745", {"start": v(-15.08, 3.84) * mm, "end": v(-15.04, 3.8) * mm});
            skLineSegment(sketch, "E746", {"start": v(-15.04, 3.8) * mm, "end": v(-15, 3.77) * mm});
            skLineSegment(sketch, "E747", {"start": v(-15, 3.77) * mm, "end": v(-14.98, 3.74) * mm});
            skLineSegment(sketch, "E748", {"start": v(-14.98, 3.74) * mm, "end": v(-14.95, 3.7) * mm});
            skLineSegment(sketch, "E749", {"start": v(-14.95, 3.7) * mm, "end": v(-14.92, 3.64) * mm});
            skLineSegment(sketch, "E750", {"start": v(-14.92, 3.64) * mm, "end": v(-14.9, 3.59) * mm});
            skLineSegment(sketch, "E751", {"start": v(-14.9, 3.59) * mm, "end": v(-14.87, 3.53) * mm});
            skLineSegment(sketch, "E752", {"start": v(-14.87, 3.53) * mm, "end": v(-14.85, 3.46) * mm});
            skLineSegment(sketch, "E753", {"start": v(-14.85, 3.46) * mm, "end": v(-14.82, 3.38) * mm});
            skLineSegment(sketch, "E754", {"start": v(-14.82, 3.38) * mm, "end": v(-14.8, 3.3) * mm});
            skLineSegment(sketch, "E755", {"start": v(-14.8, 3.3) * mm, "end": v(-14.78, 3.19) * mm});
            skLineSegment(sketch, "E756", {"start": v(-14.78, 3.19) * mm, "end": v(-14.75, 3.06) * mm});
            skLineSegment(sketch, "E757", {"start": v(-14.75, 3.06) * mm, "end": v(-14.73, 2.9) * mm});
            skLineSegment(sketch, "E758", {"start": v(-14.73, 2.9) * mm, "end": v(-14.7, 2.72) * mm});
            skLineSegment(sketch, "E759", {"start": v(-14.7, 2.72) * mm, "end": v(-14.69, 2.5) * mm});
            skLineSegment(sketch, "E760", {"start": v(-14.69, 2.5) * mm, "end": v(-14.66, 2.24) * mm});
            skLineSegment(sketch, "E761", {"start": v(-14.66, 2.24) * mm, "end": v(-14.64, 1.94) * mm});
            skLineSegment(sketch, "E762", {"start": v(-14.64, 1.94) * mm, "end": v(-14.62, 1.59) * mm});
            skLineSegment(sketch, "E763", {"start": v(-14.62, 1.59) * mm, "end": v(-14.6, 1.2) * mm});
            skLineSegment(sketch, "E764", {"start": v(-14.6, 1.2) * mm, "end": v(-14.58, 0.77) * mm});
            skLineSegment(sketch, "E765", {"start": v(-14.58, 0.77) * mm, "end": v(-14.56, 0.3) * mm});
            skLineSegment(sketch, "E766", {"start": v(-14.56, 0.3) * mm, "end": v(-14.55, -0.2) * mm});
            skLineSegment(sketch, "E767", {"start": v(-14.55, -0.2) * mm, "end": v(-14.54, -0.75) * mm});
            skLineSegment(sketch, "E768", {"start": v(-14.54, -0.75) * mm, "end": v(-14.53, -1.33) * mm});
            skLineSegment(sketch, "E769", {"start": v(-14.53, -1.33) * mm, "end": v(-14.52, -1.94) * mm});
            skLineSegment(sketch, "E770", {"start": v(-14.52, -1.94) * mm, "end": v(-14.52, -2.56) * mm});
            skLineSegment(sketch, "E771", {"start": v(-14.52, -2.56) * mm, "end": v(-14.53, -3.2) * mm});
            skLineSegment(sketch, "E772", {"start": v(-14.53, -3.2) * mm, "end": v(-14.53, -3.82) * mm});
            skLineSegment(sketch, "E773", {"start": v(-14.53, -3.82) * mm, "end": v(-14.53, -4.4) * mm});
            skLineSegment(sketch, "E774", {"start": v(-14.53, -4.4) * mm, "end": v(-14.53, -4.96) * mm});
            skLineSegment(sketch, "E775", {"start": v(-14.53, -4.96) * mm, "end": v(-14.53, -5.45) * mm});
            skLineSegment(sketch, "E776", {"start": v(-14.53, -5.45) * mm, "end": v(-14.53, -5.91) * mm});
            skLineSegment(sketch, "E777", {"start": v(-14.53, -5.91) * mm, "end": v(-15.4, -5.91) * mm});
            skCircle(sketch, "E778", {"center": v(-27.89, -2.18) * mm, "radius": 0.8 * mm});
            skCircle(sketch, "E779", {"center": v(-28.8, 1.71) * mm, "radius": 0.8 * mm});
            skCircle(sketch, "E780", {"center": v(-31.33, 4.83) * mm, "radius": 0.8 * mm});
            skCircle(sketch, "E781", {"center": v(-34.95, 6.54) * mm, "radius": 0.8 * mm});
            skCircle(sketch, "E782", {"center": v(-38.95, 6.5) * mm, "radius": 0.8 * mm});
            skCircle(sketch, "E783", {"center": v(-42.55, 4.74) * mm, "radius": 0.8 * mm});
            skCircle(sketch, "E784", {"center": v(-45.02, 1.6) * mm, "radius": 0.8 * mm});
            skCircle(sketch, "E785", {"center": v(-45.88, -2.31) * mm, "radius": 0.8 * mm});
            skCircle(sketch, "E786", {"center": v(-44.96, -6.21) * mm, "radius": 0.8 * mm});
            skCircle(sketch, "E787", {"center": v(-42.44, -9.32) * mm, "radius": 0.8 * mm});
            skCircle(sketch, "E788", {"center": v(-38.82, -11.04) * mm, "radius": 0.8 * mm});
            skCircle(sketch, "E789", {"center": v(-34.82, -11) * mm, "radius": 0.8 * mm});
            skCircle(sketch, "E790", {"center": v(-31.22, -9.24) * mm, "radius": 0.8 * mm});
            skCircle(sketch, "E791", {"center": v(-28.75, -6.1) * mm, "radius": 0.8 * mm});
            skLineSegment(sketch, "E792", {"start": v(-15.95, -15.76) * mm, "end": v(-15.85, -15.76) * mm});
            skLineSegment(sketch, "E793", {"start": v(-37.93, -9.47) * mm, "end": v(-37.93, -10) * mm});
            skLineSegment(sketch, "E794", {"start": v(-35.84, -9.47) * mm, "end": v(-35.84, -10) * mm});
            skLineSegment(sketch, "E795", {"start": v(-15.95, 3.3) * mm, "end": v(-15.85, 3.3) * mm});
            skLineSegment(sketch, "E796", {"start": v(-15.4, -5.91) * mm, "end": v(-15.4, 2.85) * mm});
            skArc(sketch, "E797", {"start": v(25.28, 0.76) * mm, "mid": v(13.08, -2.25) * mm, "end": v(25.28, -5.26) * mm});
            skLineSegment(sketch, "E798", {"start": v(-37.93, -10) * mm, "end": v(-35.84, -10) * mm});
            skCircle(sketch, "E799", {"center": v(35.38, -12.11) * mm, "radius": 0.94 * mm});
            skArc(sketch, "E800", {"start": v(33.99, -10.93) * mm, "mid": v(35.38, -13.94) * mm, "end": v(36.79, -10.94) * mm});
            skArc(sketch, "E801", {"start": v(33.99, -10.93) * mm, "mid": v(34.05, -10.84) * mm, "end": v(34.09, -10.74) * mm});
            skCircle(sketch, "E802", {"center": v(35.4, -6.36) * mm, "radius": 0.94 * mm});
            skArc(sketch, "E803", {"start": v(36.8, -7.54) * mm, "mid": v(37.22, -6.12) * mm, "end": v(36.44, -4.86) * mm});
            skArc(sketch, "E804", {"start": v(34.37, -4.85) * mm, "mid": v(33.6, -6.1) * mm, "end": v(34, -7.53) * mm});
            skArc(sketch, "E805", {"start": v(34.09, -10.74) * mm, "mid": v(34.35, -9.23) * mm, "end": v(34.1, -7.72) * mm});
            skArc(sketch, "E806", {"start": v(34.1, -7.72) * mm, "mid": v(34.06, -7.62) * mm, "end": v(34, -7.53) * mm});
            skArc(sketch, "E807", {"start": v(36.7, -7.73) * mm, "mid": v(36.44, -9.24) * mm, "end": v(36.69, -10.75) * mm});
            skArc(sketch, "E808", {"start": v(36.69, -10.75) * mm, "mid": v(36.73, -10.85) * mm, "end": v(36.79, -10.94) * mm});
            skArc(sketch, "E809", {"start": v(36.8, -7.54) * mm, "mid": v(36.74, -7.63) * mm, "end": v(36.7, -7.73) * mm});
            skCircle(sketch, "E810", {"center": v(35.42, -0.62) * mm, "radius": 0.94 * mm});
            skArc(sketch, "E811", {"start": v(34.03, 0.56) * mm, "mid": v(33.61, -0.86) * mm, "end": v(34.38, -2.12) * mm});
            skArc(sketch, "E812", {"start": v(36.45, -2.13) * mm, "mid": v(37.24, -0.87) * mm, "end": v(36.83, 0.55) * mm});
            skArc(sketch, "E813", {"start": v(34.03, 0.56) * mm, "mid": v(34.09, 0.65) * mm, "end": v(34.13, 0.75) * mm});
            skCircle(sketch, "E814", {"center": v(35.45, 5.13) * mm, "radius": 0.94 * mm});
            skArc(sketch, "E815", {"start": v(36.84, 3.95) * mm, "mid": v(37.17, 4.51) * mm, "end": v(37.27, 5.15) * mm});
            skArc(sketch, "E816", {"start": v(36.09, 6.84) * mm, "mid": v(33.96, 6.2) * mm, "end": v(34.04, 3.96) * mm});
            skArc(sketch, "E817", {"start": v(34.13, 0.75) * mm, "mid": v(34.39, 2.26) * mm, "end": v(34.14, 3.77) * mm});
            skArc(sketch, "E818", {"start": v(34.14, 3.77) * mm, "mid": v(34.1, 3.87) * mm, "end": v(34.04, 3.96) * mm});
            skArc(sketch, "E819", {"start": v(36.74, 3.77) * mm, "mid": v(36.48, 2.25) * mm, "end": v(36.73, 0.74) * mm});
            skArc(sketch, "E820", {"start": v(36.73, 0.74) * mm, "mid": v(36.77, 0.64) * mm, "end": v(36.83, 0.55) * mm});
            skArc(sketch, "E821", {"start": v(36.84, 3.95) * mm, "mid": v(36.78, 3.86) * mm, "end": v(36.74, 3.77) * mm});
            skArc(sketch, "E822", {"start": v(34.37, -4.85) * mm, "mid": v(34.58, -3.49) * mm, "end": v(34.38, -2.12) * mm});
            skArc(sketch, "E823", {"start": v(36.45, -2.13) * mm, "mid": v(36.25, -3.5) * mm, "end": v(36.44, -4.86) * mm});
            skArc(sketch, "E824", {"start": v(36.09, 6.84) * mm, "mid": v(37.32, 7.46) * mm, "end": v(38.33, 8.4) * mm});
            skArc(sketch, "E825", {"start": v(39.51, 6.71) * mm, "mid": v(38.28, 6.1) * mm, "end": v(37.27, 5.15) * mm});
            skCircle(sketch, "E826", {"center": v(40.16, 8.42) * mm, "radius": 0.94 * mm});
            skArc(sketch, "E827", {"start": v(41.89, 9.02) * mm, "mid": v(39.85, 10.23) * mm, "end": v(38.33, 8.4) * mm});
            skArc(sketch, "E828", {"start": v(39.51, 6.71) * mm, "mid": v(39.98, 6.6) * mm, "end": v(40.45, 6.62) * mm});
            skArc(sketch, "E829", {"start": v(41.89, 9.02) * mm, "mid": v(41.93, 8.93) * mm, "end": v(42, 8.84) * mm});
            skCircle(sketch, "E830", {"center": v(45.1, 5.48) * mm, "radius": 0.94 * mm});
            skArc(sketch, "E831", {"start": v(43.37, 4.87) * mm, "mid": v(43.58, 4.45) * mm, "end": v(43.9, 4.09) * mm});
            skArc(sketch, "E832", {"start": v(45.96, 3.86) * mm, "mid": v(46.83, 6.06) * mm, "end": v(44.8, 7.28) * mm});
            skArc(sketch, "E833", {"start": v(43.37, 4.87) * mm, "mid": v(43.33, 4.96) * mm, "end": v(43.28, 5.03) * mm});
            skArc(sketch, "E834", {"start": v(42, 8.84) * mm, "mid": v(43.18, 7.84) * mm, "end": v(44.62, 7.29) * mm});
            skArc(sketch, "E835", {"start": v(44.62, 7.29) * mm, "mid": v(44.71, 7.28) * mm, "end": v(44.8, 7.28) * mm});
            skArc(sketch, "E836", {"start": v(43.28, 5.03) * mm, "mid": v(42.1, 6.04) * mm, "end": v(40.66, 6.6) * mm});
            skArc(sketch, "E837", {"start": v(40.66, 6.6) * mm, "mid": v(40.56, 6.62) * mm, "end": v(40.45, 6.62) * mm});
            skCircle(sketch, "E838", {"center": v(44.47, -0.24) * mm, "radius": 0.94 * mm});
            skArc(sketch, "E839", {"start": v(44.43, -2.07) * mm, "mid": v(46.17, -0.9) * mm, "end": v(45.66, 1.15) * mm});
            skArc(sketch, "E840", {"start": v(43.6, 1.37) * mm, "mid": v(43, 0.85) * mm, "end": v(42.67, 0.12) * mm});
            skCircle(sketch, "E841", {"center": v(39.98, -3.83) * mm, "radius": 0.94 * mm});
            skArc(sketch, "E842", {"start": v(40.02, -2) * mm, "mid": v(38.16, -3.96) * mm, "end": v(40.28, -5.64) * mm});
            skArc(sketch, "E843", {"start": v(44.24, -2.1) * mm, "mid": v(42.89, -2.84) * mm, "end": v(41.86, -4) * mm});
            skArc(sketch, "E844", {"start": v(44.43, -2.07) * mm, "mid": v(44.33, -2.07) * mm, "end": v(44.24, -2.1) * mm});
            skArc(sketch, "E845", {"start": v(41.86, -4) * mm, "mid": v(41.8, -4.1) * mm, "end": v(41.77, -4.2) * mm});
            skArc(sketch, "E846", {"start": v(40.23, -1.97) * mm, "mid": v(41.58, -1.21) * mm, "end": v(42.6, -0.05) * mm});
            skArc(sketch, "E847", {"start": v(42.6, -0.05) * mm, "mid": v(42.65, 0.03) * mm, "end": v(42.67, 0.12) * mm});
            skArc(sketch, "E848", {"start": v(40.02, -2) * mm, "mid": v(40.13, -2) * mm, "end": v(40.23, -1.97) * mm});
            skArc(sketch, "E849", {"start": v(45.96, 3.86) * mm, "mid": v(45.61, 2.53) * mm, "end": v(45.66, 1.15) * mm});
            skArc(sketch, "E850", {"start": v(43.6, 1.37) * mm, "mid": v(43.95, 2.71) * mm, "end": v(43.9, 4.09) * mm});
            skCircle(sketch, "E851", {"center": v(47.94, -12.13) * mm, "radius": 0.94 * mm});
            skArc(sketch, "E852", {"start": v(46.11, -12.25) * mm, "mid": v(49.2, -13.45) * mm, "end": v(48.13, -10.31) * mm});
            skArc(sketch, "E853", {"start": v(46.11, -12.25) * mm, "mid": v(46.1, -12.15) * mm, "end": v(46.05, -12.05) * mm});
            skCircle(sketch, "E854", {"center": v(43.96, -7.98) * mm, "radius": 0.94 * mm});
            skArc(sketch, "E855", {"start": v(45.78, -7.86) * mm, "mid": v(45.1, -6.55) * mm, "end": v(43.66, -6.18) * mm});
            skArc(sketch, "E856", {"start": v(42.17, -7.61) * mm, "mid": v(42.48, -9.06) * mm, "end": v(43.76, -9.8) * mm});
            skArc(sketch, "E857", {"start": v(46.05, -12.05) * mm, "mid": v(45.2, -10.78) * mm, "end": v(43.96, -9.87) * mm});
            skArc(sketch, "E858", {"start": v(43.96, -9.87) * mm, "mid": v(43.86, -9.82) * mm, "end": v(43.76, -9.8) * mm});
            skArc(sketch, "E859", {"start": v(45.84, -8.07) * mm, "mid": v(46.7, -9.33) * mm, "end": v(47.93, -10.25) * mm});
            skArc(sketch, "E860", {"start": v(47.93, -10.25) * mm, "mid": v(48.03, -10.3) * mm, "end": v(48.13, -10.31) * mm});
            skArc(sketch, "E861", {"start": v(45.78, -7.86) * mm, "mid": v(45.8, -7.97) * mm, "end": v(45.84, -8.07) * mm});
            skArc(sketch, "E862", {"start": v(42.17, -7.61) * mm, "mid": v(41.37, -6.49) * mm, "end": v(40.28, -5.64) * mm});
            skArc(sketch, "E863", {"start": v(41.77, -4.2) * mm, "mid": v(42.57, -5.33) * mm, "end": v(43.66, -6.18) * mm});
            skLineSegment(sketch, "E864", {"start": v(0.42, -9.53) * mm, "end": v(0.42, -10.22) * mm});
            skLineSegment(sketch, "E865", {"start": v(-0.52, -9.46) * mm, "end": v(-0.52, -10.17) * mm});
            skLineSegment(sketch, "E866", {"start": v(-15.96, 9) * mm, "end": v(-15.95, 9) * mm});
            skText(sketch, "E867", { "text": "2017", "fontName": "NotoSans-Bold.ttf"});
            const initialGuessF0  = {"E867": [0.03626, -0.02302, 1, 0, 0.00476]};
            skSetInitialGuess(sketch, initialGuessF0);
            skSolve(sketch);
        }
        {
            var Q0;
            Q0=qCreatedBy(makeId("Top.planeOp"),FACE);
            var sketch = newSketch(context, id + "F1", { "sketchPlane" : qUnion([Q0])});
            skLineSegment(sketch, "E868", {"start": v(54.77, -22.46) * mm, "end": v(54.77, 22.46) * mm});
            skArc(sketch, "E869", {"start": v(54.77, 22.46) * mm, "mid": v(53.68, 25.11) * mm, "end": v(51.02, 26.21) * mm});
            skLineSegment(sketch, "E870", {"start": v(51.02, 26.21) * mm, "end": v(-51.02, 26.21) * mm});
            skArc(sketch, "E871", {"start": v(-51.02, 26.21) * mm, "mid": v(-53.68, 25.11) * mm, "end": v(-54.77, 22.46) * mm});
            skLineSegment(sketch, "E872", {"start": v(-54.77, 22.46) * mm, "end": v(-54.77, -22.46) * mm});
            skArc(sketch, "E873", {"start": v(-54.77, -22.46) * mm, "mid": v(-53.68, -25.11) * mm, "end": v(-51.02, -26.21) * mm});
            skLineSegment(sketch, "E874", {"start": v(-51.02, -26.21) * mm, "end": v(51.02, -26.21) * mm});
            skArc(sketch, "E875", {"start": v(51.02, -26.21) * mm, "mid": v(53.68, -25.11) * mm, "end": v(54.77, -22.46) * mm});
            skLineSegment(sketch, "E876.0", {"start": v(50.96, 24.94) * mm, "end": v(-50.96, 24.94) * mm, "construction": true});
            skLineSegment(sketch, "E876.1", {"start": v(53.5, -22.4) * mm, "end": v(53.5, 22.4) * mm, "construction": true});
            skLineSegment(sketch, "E876.2", {"start": v(-50.96, -24.94) * mm, "end": v(50.96, -24.94) * mm, "construction": true});
            skLineSegment(sketch, "E876.3", {"start": v(-53.5, 22.4) * mm, "end": v(-53.5, -22.4) * mm, "construction": true});
            skPoint(sketch, "E877.visualSharp", {"position": v(-53.5, 24.94) * mm});
            skArc(sketch, "E877.filletArc", {"start": v(-50.96, 24.94) * mm, "mid": v(-52.76, 24.2) * mm, "end": v(-53.5, 22.4) * mm, "construction": true});
            skPoint(sketch, "E878.visualSharp", {"position": v(-53.5, -24.94) * mm});
            skArc(sketch, "E878.filletArc", {"start": v(-53.5, -22.4) * mm, "mid": v(-52.76, -24.2) * mm, "end": v(-50.96, -24.94) * mm, "construction": true});
            skPoint(sketch, "E879.visualSharp", {"position": v(53.5, -24.94) * mm});
            skArc(sketch, "E879.filletArc", {"start": v(50.96, -24.94) * mm, "mid": v(52.76, -24.2) * mm, "end": v(53.5, -22.4) * mm, "construction": true});
            skPoint(sketch, "E880.visualSharp", {"position": v(53.5, 24.94) * mm});
            skArc(sketch, "E880.filletArc", {"start": v(53.5, 22.4) * mm, "mid": v(52.76, 24.2) * mm, "end": v(50.96, 24.94) * mm, "construction": true});
            skSolve(sketch);
        }
        {
            var Q0;
            {var subQ3=sQuery(id+"F0.wireOp",EDGE,"E1");Q0=makeQuery(id+"F0.imprint","IMPRINT",FACE,{"disambiguationData":[TD([[makeQuery(id+"F0.imprint","IMPRINT",EDGE,{"derivedFrom":subQ3}),1.0]])]});}
            var Q1;
            {var subQ7=sQuery(id+"F0.wireOp",EDGE,"E162");Q1=makeQuery(id+"F0.imprint","IMPRINT",FACE,{"disambiguationData":[TD([[makeQuery(id+"F0.imprint","IMPRINT",EDGE,{"derivedFrom":subQ7}),1.0]])]});}
            var Q2;
            {var subQ4=sQuery(id+"F0.wireOp",EDGE,"E485");Q2=makeQuery(id+"F0.imprint","IMPRINT",FACE,{"disambiguationData":[TD([[makeQuery(id+"F0.imprint","IMPRINT",EDGE,{"derivedFrom":subQ4}),-1.0]])]});}
            var Q3;
            {var subQ4=sQuery(id+"F0.wireOp",EDGE,"E176");Q3=makeQuery(id+"F0.imprint","IMPRINT",FACE,{"disambiguationData":[TD([[makeQuery(id+"F0.imprint","IMPRINT",EDGE,{"derivedFrom":subQ4}),1.0]])]});}
            var Q4;
            Q4=makeQuery(id+"F0.imprint","IMPRINT",FACE,{"disambiguationData":[TD([[makeQuery(id+"F0.imprint","IMPRINT",EDGE,{"derivedFrom":sQuery(id+"F0.wireOp",EDGE,"E125")}),1.0]])]});
            var Q5;
            Q5=makeQuery(id+"F0.imprint","IMPRINT",FACE,{"disambiguationData":[TD([[makeQuery(id+"F0.imprint","IMPRINT",EDGE,{"derivedFrom":sQuery(id+"F0.wireOp",EDGE,"E64")}),1.0]])]});
            var Q6;
            Q6=makeQuery(id+"F0.imprint","IMPRINT",FACE,{"disambiguationData":[TD([[makeQuery(id+"F0.imprint","IMPRINT",EDGE,{"derivedFrom":sQuery(id+"F0.wireOp",EDGE,"E122")}),1.0]])]});
            var Q7;
            Q7=makeQuery(id+"F0.imprint","IMPRINT",FACE,{"disambiguationData":[TD([[makeQuery(id+"F0.imprint","IMPRINT",EDGE,{"derivedFrom":sQuery(id+"F0.wireOp",EDGE,"E121")}),-1.0]])]});
            var Q8;
            Q8=makeQuery(id+"F0.imprint","IMPRINT",FACE,{"disambiguationData":[TD([[makeQuery(id+"F0.imprint","IMPRINT",EDGE,{"derivedFrom":sQuery(id+"F0.wireOp",EDGE,"E799")}),1.0]])]});
            var Q9;
            Q9=makeQuery(id+"F0.imprint","IMPRINT",FACE,{"disambiguationData":[TD([[makeQuery(id+"F0.imprint","IMPRINT",EDGE,{"derivedFrom":sQuery(id+"F0.wireOp",EDGE,"1c2054f4-1edd-4350-a152-99b7c5aa451a.sketch_text.stroke-0")}),-1.0]])]});
            var Q10;
            Q10=makeQuery(id+"F0.imprint","IMPRINT",FACE,{"disambiguationData":[TD([[makeQuery(id+"F0.imprint","IMPRINT",EDGE,{"derivedFrom":sQuery(id+"F0.wireOp",EDGE,"1c2054f4-1edd-4350-a152-99b7c5aa451a.sketch_text.stroke-24")}),-1.0]])]});
            var Q11;
            Q11=makeQuery(id+"F0.imprint","IMPRINT",FACE,{"disambiguationData":[TD([[makeQuery(id+"F0.imprint","IMPRINT",EDGE,{"derivedFrom":sQuery(id+"F0.wireOp",EDGE,"1c2054f4-1edd-4350-a152-99b7c5aa451a.sketch_text.stroke-40")}),-1.0]])]});
            var Q12;
            Q12=makeQuery(id+"F0.imprint","IMPRINT",FACE,{"disambiguationData":[TD([[makeQuery(id+"F0.imprint","IMPRINT",EDGE,{"derivedFrom":sQuery(id+"F0.wireOp",EDGE,"1c2054f4-1edd-4350-a152-99b7c5aa451a.sketch_text.stroke-50")}),-1.0]])]});
            var Q13;
            Q13=makeQuery(id+"F0.imprint","IMPRINT",FACE,{"disambiguationData":[TD([[makeQuery(id+"F0.imprint","IMPRINT",EDGE,{"derivedFrom":sQuery(id+"F0.wireOp",EDGE,"E867.sketch_text.stroke-0")}),-1.0]])]});
            var Q14;
            Q14=makeQuery(id+"F0.imprint","IMPRINT",FACE,{"disambiguationData":[TD([[makeQuery(id+"F0.imprint","IMPRINT",EDGE,{"derivedFrom":sQuery(id+"F0.wireOp",EDGE,"E867.sketch_text.stroke-24")}),-1.0]])]});
            var Q15;
            Q15=makeQuery(id+"F0.imprint","IMPRINT",FACE,{"disambiguationData":[TD([[makeQuery(id+"F0.imprint","IMPRINT",EDGE,{"derivedFrom":sQuery(id+"F0.wireOp",EDGE,"E867.sketch_text.stroke-40")}),-1.0]])]});
            var Q16;
            Q16=makeQuery(id+"F0.imprint","IMPRINT",FACE,{"disambiguationData":[TD([[makeQuery(id+"F0.imprint","IMPRINT",EDGE,{"derivedFrom":sQuery(id+"F0.wireOp",EDGE,"E867.sketch_text.stroke-50")}),-1.0]])]});
            extrude(context, id + "F2", {"entities" : qUnion([Q0, Q1, Q2, Q3, Q4, Q5, Q6, Q7, Q8, Q9, Q10, Q11, Q12, Q13, Q14, Q15, Q16]), "depth" : 1.52 * mm, "offsetDistance" : 25.4 * mm});
        }
        {
            var Q0;
            Q0=qSketchRegion(id+"F1",true);
            extrude(context, id + "F3", {"entities" : qUnion([Q0]), "operationType" : NewBodyOperationType.ADD, "oppositeDirection" : true, "depth" : 2.38 * mm, "offsetDistance" : 25.4 * mm});
        }
        {
            var Q0;
            {var subQ58=sQuery(id+"F0.wireOp",EDGE,"E0");var subQ59=sQuery(id+"F1.wireOp",EDGE,"E868");var subQ60=sQuery(id+"F1.wireOp",EDGE,"E869");var subQ61=sQuery(id+"F1.wireOp",EDGE,"E872");var subQ62=sQuery(id+"F1.wireOp",EDGE,"E873");var subQ63=sQuery(id+"F1.wireOp",EDGE,"E874");var subQ64=sQuery(id+"F1.wireOp",EDGE,"E875");Q0=makeQuery(id+"F3.boolean.opBoolean","SPLIT",FACE,{"disambiguationData":[TD([makeQuery(id+"F2.opExtrude","SWEPT_FACE",FACE,{"disambiguationData":[OSD([subQ58])]})])],"derivedFrom":makeQuery(id+"F3.opExtrude","CAP_FACE",FACE,{"disambiguationData":[OSD([subQ59,subQ60,sQuery(id+"F1.wireOp",EDGE,"E870"),sQuery(id+"F1.wireOp",EDGE,"E871"),subQ61,subQ62,subQ63,subQ64])],"isStart":true})});}
            var sketch = newSketch(context, id + "F4", { "sketchPlane" : qUnion([Q0])});
            skLineSegment(sketch, "E881", {"start": v(54.77, -22.46) * mm, "end": v(54.77, 12.06) * mm});
            skLineSegment(sketch, "E882", {"start": v(-54.77, 12.13) * mm, "end": v(-54.77, -22.46) * mm});
            skArc(sketch, "E883", {"start": v(-54.77, -22.46) * mm, "mid": v(-53.68, -25.11) * mm, "end": v(-51.02, -26.21) * mm});
            skLineSegment(sketch, "E884", {"start": v(-51.02, -26.21) * mm, "end": v(51.02, -26.21) * mm});
            skArc(sketch, "E885", {"start": v(51.02, -26.21) * mm, "mid": v(53.68, -25.11) * mm, "end": v(54.77, -22.46) * mm});
            skLineSegment(sketch, "E886.1", {"start": v(53.5, -22.4) * mm, "end": v(53.5, 13.14) * mm});
            skLineSegment(sketch, "E886.2", {"start": v(-50.96, -24.94) * mm, "end": v(50.96, -24.94) * mm});
            skLineSegment(sketch, "E886.3", {"start": v(-53.5, 12.9) * mm, "end": v(-53.5, -22.4) * mm});
            skPoint(sketch, "E887.visualSharp", {"position": v(-53.5, 24.94) * mm});
            skPoint(sketch, "E888.visualSharp", {"position": v(-53.5, -24.94) * mm});
            skArc(sketch, "E888.filletArc", {"start": v(-53.5, -22.4) * mm, "mid": v(-52.76, -24.2) * mm, "end": v(-50.96, -24.94) * mm});
            skPoint(sketch, "E889.visualSharp", {"position": v(53.5, -24.94) * mm});
            skArc(sketch, "E889.filletArc", {"start": v(50.96, -24.94) * mm, "mid": v(52.76, -24.2) * mm, "end": v(53.5, -22.4) * mm});
            skPoint(sketch, "E890.visualSharp", {"position": v(53.5, 24.94) * mm});
            skLineSegment(sketch, "E891", {"start": v(-54.77, 12.13) * mm, "end": v(-53.5, 12.9) * mm});
            skLineSegment(sketch, "E892", {"start": v(53.5, 13.14) * mm, "end": v(53.78, 12.92) * mm});
            skLineSegment(sketch, "E893", {"start": v(53.78, 12.92) * mm, "end": v(54.77, 12.06) * mm});
            skSolve(sketch);
        }
        {
            var Q0;
            Q0=qSketchRegion(id+"F4",true);
            extrude(context, id + "F5", {"entities" : qUnion([Q0]), "operationType" : NewBodyOperationType.ADD, "depth" : 1.52 * mm, "offsetDistance" : 25.4 * mm});
        }
        {
            var Q0;
            Q0=makeQuery(id+"F5.boolean.opBoolean","MERGE",FACE,{"derivedFrom":[makeQuery(id+"F2.opExtrude","CAP_FACE",FACE,{"disambiguationData":[OSD([sQuery(id+"F0.wireOp",EDGE,"E0"),sQuery(id+"F0.wireOp",EDGE,"E1"),sQuery(id+"F0.wireOp",EDGE,"E2"),sQuery(id+"F0.wireOp",EDGE,"E3"),sQuery(id+"F0.wireOp",EDGE,"E4"),sQuery(id+"F0.wireOp",EDGE,"E8"),sQuery(id+"F0.wireOp",EDGE,"E9"),sQuery(id+"F0.wireOp",EDGE,"E10"),sQuery(id+"F0.wireOp",EDGE,"E11"),sQuery(id+"F0.wireOp",EDGE,"E12"),sQuery(id+"F0.wireOp",EDGE,"E13"),sQuery(id+"F0.wireOp",EDGE,"E14"),sQuery(id+"F0.wireOp",EDGE,"E15"),sQuery(id+"F0.wireOp",EDGE,"E16"),sQuery(id+"F0.wireOp",EDGE,"E17"),sQuery(id+"F0.wireOp",EDGE,"E18"),sQuery(id+"F0.wireOp",EDGE,"E19"),sQuery(id+"F0.wireOp",EDGE,"E20"),sQuery(id+"F0.wireOp",EDGE,"E21"),sQuery(id+"F0.wireOp",EDGE,"E22"),sQuery(id+"F0.wireOp",EDGE,"E23"),sQuery(id+"F0.wireOp",EDGE,"E24"),sQuery(id+"F0.wireOp",EDGE,"E25"),sQuery(id+"F0.wireOp",EDGE,"E26"),sQuery(id+"F0.wireOp",EDGE,"E27"),sQuery(id+"F0.wireOp",EDGE,"E28"),sQuery(id+"F0.wireOp",EDGE,"E29"),sQuery(id+"F0.wireOp",EDGE,"E30"),sQuery(id+"F0.wireOp",EDGE,"E31"),sQuery(id+"F0.wireOp",EDGE,"E32"),sQuery(id+"F0.wireOp",EDGE,"E33"),sQuery(id+"F0.wireOp",EDGE,"E34"),sQuery(id+"F0.wireOp",EDGE,"E35"),sQuery(id+"F0.wireOp",EDGE,"E36"),sQuery(id+"F0.wireOp",EDGE,"E37"),sQuery(id+"F0.wireOp",EDGE,"E38"),sQuery(id+"F0.wireOp",EDGE,"E39"),sQuery(id+"F0.wireOp",EDGE,"E40"),sQuery(id+"F0.wireOp",EDGE,"E41"),sQuery(id+"F0.wireOp",EDGE,"E42"),sQuery(id+"F0.wireOp",EDGE,"E43"),sQuery(id+"F0.wireOp",EDGE,"E44"),sQuery(id+"F0.wireOp",EDGE,"E45"),sQuery(id+"F0.wireOp",EDGE,"E46"),sQuery(id+"F0.wireOp",EDGE,"E47"),sQuery(id+"F0.wireOp",EDGE,"E48"),sQuery(id+"F0.wireOp",EDGE,"E49"),sQuery(id+"F0.wireOp",EDGE,"E50"),sQuery(id+"F0.wireOp",EDGE,"E51"),sQuery(id+"F0.wireOp",EDGE,"E52"),sQuery(id+"F0.wireOp",EDGE,"E53"),sQuery(id+"F0.wireOp",EDGE,"E54"),sQuery(id+"F0.wireOp",EDGE,"E55"),sQuery(id+"F0.wireOp",EDGE,"E56"),sQuery(id+"F0.wireOp",EDGE,"E57"),sQuery(id+"F0.wireOp",EDGE,"E58"),sQuery(id+"F0.wireOp",EDGE,"E59"),sQuery(id+"F0.wireOp",EDGE,"E60"),sQuery(id+"F0.wireOp",EDGE,"E61"),sQuery(id+"F0.wireOp",EDGE,"E62"),sQuery(id+"F0.wireOp",EDGE,"E63")])],"isStart":false}),makeQuery(id+"F5.opExtrude","CAP_FACE",FACE,{"disambiguationData":[OSD([sQuery(id+"F4.wireOp",EDGE,"E881"),sQuery(id+"F4.wireOp",EDGE,"E882"),sQuery(id+"F4.wireOp",EDGE,"E883"),sQuery(id+"F4.wireOp",EDGE,"E884"),sQuery(id+"F4.wireOp",EDGE,"E885"),sQuery(id+"F4.wireOp",EDGE,"E886.1"),sQuery(id+"F4.wireOp",EDGE,"E886.2"),sQuery(id+"F4.wireOp",EDGE,"E886.3"),sQuery(id+"F4.wireOp",EDGE,"E888.filletArc"),sQuery(id+"F4.wireOp",EDGE,"E889.filletArc"),sQuery(id+"F4.wireOp",EDGE,"E891"),sQuery(id+"F4.wireOp",EDGE,"E892"),sQuery(id+"F4.wireOp",EDGE,"E893")])],"isStart":false})]});
            var sketch = newSketch(context, id + "F6", { "sketchPlane" : qUnion([Q0])});
            skLineSegment(sketch, "E894.bottom", {"start": v(-34.45, 23.83) * mm, "end": v(-29.7, 23.83) * mm});
            skLineSegment(sketch, "E894.top", {"start": v(-34.45, 21.45) * mm, "end": v(-29.7, 21.45) * mm});
            skLineSegment(sketch, "E894.left", {"start": v(-34.45, 23.83) * mm, "end": v(-34.45, 21.45) * mm});
            skLineSegment(sketch, "E894.right", {"start": v(-29.7, 23.83) * mm, "end": v(-29.7, 21.45) * mm});
            skLineSegment(sketch, "E895", {"start": v(0, 26.21) * mm, "end": v(0, -26.21) * mm, "construction": true});
            skLineSegment(sketch, "E896.MirrorCS", {"start": v(34.45, 23.83) * mm, "end": v(34.45, 21.45) * mm});
            skLineSegment(sketch, "E897.MirrorCS", {"start": v(29.7, 23.83) * mm, "end": v(29.7, 21.45) * mm});
            skLineSegment(sketch, "E898.MirrorCS", {"start": v(34.45, 21.45) * mm, "end": v(29.7, 21.45) * mm});
            skLineSegment(sketch, "E899.MirrorCS", {"start": v(34.45, 23.83) * mm, "end": v(29.7, 23.83) * mm});
            skLineSegment(sketch, "E900", {"start": v(0, 0) * mm, "end": v(-59.23, 0) * mm, "construction": true});
            skLineSegment(sketch, "E901", {"start": v(0, 0) * mm, "end": v(56.47, 0) * mm, "construction": true});
            skLineSegment(sketch, "E902.MirrorCS", {"start": v(-34.45, -23.83) * mm, "end": v(-29.7, -23.83) * mm});
            skLineSegment(sketch, "E903.MirrorCS", {"start": v(-34.45, -23.83) * mm, "end": v(-34.45, -21.45) * mm});
            skLineSegment(sketch, "E904.MirrorCS", {"start": v(-34.45, -21.45) * mm, "end": v(-29.7, -21.45) * mm});
            skLineSegment(sketch, "E905.MirrorCS", {"start": v(-29.7, -23.83) * mm, "end": v(-29.7, -21.45) * mm});
            skLineSegment(sketch, "E906.MirrorCS", {"start": v(29.7, -23.83) * mm, "end": v(29.7, -21.45) * mm});
            skLineSegment(sketch, "E907.MirrorCS", {"start": v(34.45, -23.83) * mm, "end": v(29.7, -23.83) * mm});
            skLineSegment(sketch, "E908.MirrorCS", {"start": v(34.45, -23.83) * mm, "end": v(34.45, -21.45) * mm});
            skLineSegment(sketch, "E909.MirrorCS", {"start": v(34.45, -21.45) * mm, "end": v(29.7, -21.45) * mm});
            skSolve(sketch);
        }
        {
            var Q0;
            Q0 = qSketchRegion(id + "F6", true);
            extrude(context, id + "F7", {"entities" : qUnion([Q0]), "operationType" : NewBodyOperationType.REMOVE, "endBound" : BoundingType.THROUGH_ALL, "oppositeDirection" : true, "depth" : 25.4 * mm, "offsetDistance" : 25.4 * mm});
        }
        {
            var Q0;
            Q0=makeQuery(id+"F5.boolean.opBoolean","MERGE",FACE,{"derivedFrom":[makeQuery(id+"F2.opExtrude","CAP_FACE",FACE,{"disambiguationData":[OSD([sQuery(id+"F0.wireOp",EDGE,"E0"),sQuery(id+"F0.wireOp",EDGE,"E1"),sQuery(id+"F0.wireOp",EDGE,"E2"),sQuery(id+"F0.wireOp",EDGE,"E3"),sQuery(id+"F0.wireOp",EDGE,"E4"),sQuery(id+"F0.wireOp",EDGE,"E8"),sQuery(id+"F0.wireOp",EDGE,"E9"),sQuery(id+"F0.wireOp",EDGE,"E10"),sQuery(id+"F0.wireOp",EDGE,"E11"),sQuery(id+"F0.wireOp",EDGE,"E12"),sQuery(id+"F0.wireOp",EDGE,"E13"),sQuery(id+"F0.wireOp",EDGE,"E14"),sQuery(id+"F0.wireOp",EDGE,"E15"),sQuery(id+"F0.wireOp",EDGE,"E16"),sQuery(id+"F0.wireOp",EDGE,"E17"),sQuery(id+"F0.wireOp",EDGE,"E18"),sQuery(id+"F0.wireOp",EDGE,"E19"),sQuery(id+"F0.wireOp",EDGE,"E20"),sQuery(id+"F0.wireOp",EDGE,"E21"),sQuery(id+"F0.wireOp",EDGE,"E22"),sQuery(id+"F0.wireOp",EDGE,"E23"),sQuery(id+"F0.wireOp",EDGE,"E24"),sQuery(id+"F0.wireOp",EDGE,"E25"),sQuery(id+"F0.wireOp",EDGE,"E26"),sQuery(id+"F0.wireOp",EDGE,"E27"),sQuery(id+"F0.wireOp",EDGE,"E28"),sQuery(id+"F0.wireOp",EDGE,"E29"),sQuery(id+"F0.wireOp",EDGE,"E30"),sQuery(id+"F0.wireOp",EDGE,"E31"),sQuery(id+"F0.wireOp",EDGE,"E32"),sQuery(id+"F0.wireOp",EDGE,"E33"),sQuery(id+"F0.wireOp",EDGE,"E34"),sQuery(id+"F0.wireOp",EDGE,"E35"),sQuery(id+"F0.wireOp",EDGE,"E36"),sQuery(id+"F0.wireOp",EDGE,"E37"),sQuery(id+"F0.wireOp",EDGE,"E38"),sQuery(id+"F0.wireOp",EDGE,"E39"),sQuery(id+"F0.wireOp",EDGE,"E40"),sQuery(id+"F0.wireOp",EDGE,"E41"),sQuery(id+"F0.wireOp",EDGE,"E42"),sQuery(id+"F0.wireOp",EDGE,"E43"),sQuery(id+"F0.wireOp",EDGE,"E44"),sQuery(id+"F0.wireOp",EDGE,"E45"),sQuery(id+"F0.wireOp",EDGE,"E46"),sQuery(id+"F0.wireOp",EDGE,"E47"),sQuery(id+"F0.wireOp",EDGE,"E48"),sQuery(id+"F0.wireOp",EDGE,"E49"),sQuery(id+"F0.wireOp",EDGE,"E50"),sQuery(id+"F0.wireOp",EDGE,"E51"),sQuery(id+"F0.wireOp",EDGE,"E52"),sQuery(id+"F0.wireOp",EDGE,"E53"),sQuery(id+"F0.wireOp",EDGE,"E54"),sQuery(id+"F0.wireOp",EDGE,"E55"),sQuery(id+"F0.wireOp",EDGE,"E56"),sQuery(id+"F0.wireOp",EDGE,"E57"),sQuery(id+"F0.wireOp",EDGE,"E58"),sQuery(id+"F0.wireOp",EDGE,"E59"),sQuery(id+"F0.wireOp",EDGE,"E60"),sQuery(id+"F0.wireOp",EDGE,"E61"),sQuery(id+"F0.wireOp",EDGE,"E62"),sQuery(id+"F0.wireOp",EDGE,"E63")])],"isStart":false}),makeQuery(id+"F5.opExtrude","CAP_FACE",FACE,{"disambiguationData":[OSD([sQuery(id+"F4.wireOp",EDGE,"E881"),sQuery(id+"F4.wireOp",EDGE,"E882"),sQuery(id+"F4.wireOp",EDGE,"E883"),sQuery(id+"F4.wireOp",EDGE,"E884"),sQuery(id+"F4.wireOp",EDGE,"E885"),sQuery(id+"F4.wireOp",EDGE,"E886.1"),sQuery(id+"F4.wireOp",EDGE,"E886.2"),sQuery(id+"F4.wireOp",EDGE,"E886.3"),sQuery(id+"F4.wireOp",EDGE,"E888.filletArc"),sQuery(id+"F4.wireOp",EDGE,"E889.filletArc"),sQuery(id+"F4.wireOp",EDGE,"E891"),sQuery(id+"F4.wireOp",EDGE,"E892"),sQuery(id+"F4.wireOp",EDGE,"E893")])],"isStart":false})]});
            var Q1;
            {var subQ0=sQuery(id+"F1.wireOp",EDGE,"E868");var subQ1=sQuery(id+"F1.wireOp",EDGE,"E872");var subQ2=sQuery(id+"F1.wireOp",EDGE,"E873");var subQ3=sQuery(id+"F1.wireOp",EDGE,"E874");var subQ4=sQuery(id+"F1.wireOp",EDGE,"E875");Q1=makeQuery(id+"F7.boolean.opBoolean","INTERSECT",EDGE,{"derivedFrom":[makeQuery(id+"F3.boolean.opBoolean","SPLIT",FACE,{"disambiguationData":[TD([makeQuery(id+"F2.opExtrude","SWEPT_FACE",FACE,{"disambiguationData":[OSD([sQuery(id+"F0.wireOp",EDGE,"E0")])]})])],"derivedFrom":makeQuery(id+"F3.opExtrude","CAP_FACE",FACE,{"disambiguationData":[OSD([subQ0,sQuery(id+"F1.wireOp",EDGE,"E869"),sQuery(id+"F1.wireOp",EDGE,"E870"),sQuery(id+"F1.wireOp",EDGE,"E871"),subQ1,subQ2,subQ3,subQ4])],"isStart":true})}),makeQuery(id+"F7.opExtrude","SWEPT_FACE",FACE,{"disambiguationData":[OSD([sQuery(id+"F6.wireOp",EDGE,"E904.MirrorCS")])]})]});}
            var Q2;
            {var subQ0=sQuery(id+"F1.wireOp",EDGE,"E868");var subQ1=sQuery(id+"F1.wireOp",EDGE,"E872");var subQ2=sQuery(id+"F1.wireOp",EDGE,"E873");var subQ3=sQuery(id+"F1.wireOp",EDGE,"E874");var subQ4=sQuery(id+"F1.wireOp",EDGE,"E875");Q2=makeQuery(id+"F7.boolean.opBoolean","INTERSECT",EDGE,{"derivedFrom":[makeQuery(id+"F3.boolean.opBoolean","SPLIT",FACE,{"disambiguationData":[TD([makeQuery(id+"F2.opExtrude","SWEPT_FACE",FACE,{"disambiguationData":[OSD([sQuery(id+"F0.wireOp",EDGE,"E0")])]})])],"derivedFrom":makeQuery(id+"F3.opExtrude","CAP_FACE",FACE,{"disambiguationData":[OSD([subQ0,sQuery(id+"F1.wireOp",EDGE,"E869"),sQuery(id+"F1.wireOp",EDGE,"E870"),sQuery(id+"F1.wireOp",EDGE,"E871"),subQ1,subQ2,subQ3,subQ4])],"isStart":true})}),makeQuery(id+"F7.opExtrude","SWEPT_FACE",FACE,{"disambiguationData":[OSD([sQuery(id+"F6.wireOp",EDGE,"E903.MirrorCS")])]})]});}
            var Q3;
            {var subQ0=sQuery(id+"F1.wireOp",EDGE,"E868");var subQ1=sQuery(id+"F1.wireOp",EDGE,"E872");var subQ2=sQuery(id+"F1.wireOp",EDGE,"E873");var subQ3=sQuery(id+"F1.wireOp",EDGE,"E874");var subQ4=sQuery(id+"F1.wireOp",EDGE,"E875");Q3=makeQuery(id+"F7.boolean.opBoolean","INTERSECT",EDGE,{"derivedFrom":[makeQuery(id+"F3.boolean.opBoolean","SPLIT",FACE,{"disambiguationData":[TD([makeQuery(id+"F2.opExtrude","SWEPT_FACE",FACE,{"disambiguationData":[OSD([sQuery(id+"F0.wireOp",EDGE,"E0")])]})])],"derivedFrom":makeQuery(id+"F3.opExtrude","CAP_FACE",FACE,{"disambiguationData":[OSD([subQ0,sQuery(id+"F1.wireOp",EDGE,"E869"),sQuery(id+"F1.wireOp",EDGE,"E870"),sQuery(id+"F1.wireOp",EDGE,"E871"),subQ1,subQ2,subQ3,subQ4])],"isStart":true})}),makeQuery(id+"F7.opExtrude","SWEPT_FACE",FACE,{"disambiguationData":[OSD([sQuery(id+"F6.wireOp",EDGE,"E902.MirrorCS")])]})]});}
            var Q4;
            {var subQ0=sQuery(id+"F1.wireOp",EDGE,"E868");var subQ1=sQuery(id+"F1.wireOp",EDGE,"E872");var subQ2=sQuery(id+"F1.wireOp",EDGE,"E873");var subQ3=sQuery(id+"F1.wireOp",EDGE,"E874");var subQ4=sQuery(id+"F1.wireOp",EDGE,"E875");Q4=makeQuery(id+"F7.boolean.opBoolean","INTERSECT",EDGE,{"derivedFrom":[makeQuery(id+"F3.boolean.opBoolean","SPLIT",FACE,{"disambiguationData":[TD([makeQuery(id+"F2.opExtrude","SWEPT_FACE",FACE,{"disambiguationData":[OSD([sQuery(id+"F0.wireOp",EDGE,"E0")])]})])],"derivedFrom":makeQuery(id+"F3.opExtrude","CAP_FACE",FACE,{"disambiguationData":[OSD([subQ0,sQuery(id+"F1.wireOp",EDGE,"E869"),sQuery(id+"F1.wireOp",EDGE,"E870"),sQuery(id+"F1.wireOp",EDGE,"E871"),subQ1,subQ2,subQ3,subQ4])],"isStart":true})}),makeQuery(id+"F7.opExtrude","SWEPT_FACE",FACE,{"disambiguationData":[OSD([sQuery(id+"F6.wireOp",EDGE,"E905.MirrorCS")])]})]});}
            var Q5;
            {var subQ0=sQuery(id+"F1.wireOp",EDGE,"E868");var subQ1=sQuery(id+"F1.wireOp",EDGE,"E872");var subQ2=sQuery(id+"F1.wireOp",EDGE,"E873");var subQ3=sQuery(id+"F1.wireOp",EDGE,"E874");var subQ4=sQuery(id+"F1.wireOp",EDGE,"E875");Q5=makeQuery(id+"F7.boolean.opBoolean","INTERSECT",EDGE,{"derivedFrom":[makeQuery(id+"F3.boolean.opBoolean","SPLIT",FACE,{"disambiguationData":[TD([makeQuery(id+"F2.opExtrude","SWEPT_FACE",FACE,{"disambiguationData":[OSD([sQuery(id+"F0.wireOp",EDGE,"E0")])]})])],"derivedFrom":makeQuery(id+"F3.opExtrude","CAP_FACE",FACE,{"disambiguationData":[OSD([subQ0,sQuery(id+"F1.wireOp",EDGE,"E869"),sQuery(id+"F1.wireOp",EDGE,"E870"),sQuery(id+"F1.wireOp",EDGE,"E871"),subQ1,subQ2,subQ3,subQ4])],"isStart":true})}),makeQuery(id+"F7.opExtrude","SWEPT_FACE",FACE,{"disambiguationData":[OSD([sQuery(id+"F6.wireOp",EDGE,"E906.MirrorCS")])]})]});}
            var Q6;
            {var subQ0=sQuery(id+"F1.wireOp",EDGE,"E868");var subQ1=sQuery(id+"F1.wireOp",EDGE,"E872");var subQ2=sQuery(id+"F1.wireOp",EDGE,"E873");var subQ3=sQuery(id+"F1.wireOp",EDGE,"E874");var subQ4=sQuery(id+"F1.wireOp",EDGE,"E875");Q6=makeQuery(id+"F7.boolean.opBoolean","INTERSECT",EDGE,{"derivedFrom":[makeQuery(id+"F3.boolean.opBoolean","SPLIT",FACE,{"disambiguationData":[TD([makeQuery(id+"F2.opExtrude","SWEPT_FACE",FACE,{"disambiguationData":[OSD([sQuery(id+"F0.wireOp",EDGE,"E0")])]})])],"derivedFrom":makeQuery(id+"F3.opExtrude","CAP_FACE",FACE,{"disambiguationData":[OSD([subQ0,sQuery(id+"F1.wireOp",EDGE,"E869"),sQuery(id+"F1.wireOp",EDGE,"E870"),sQuery(id+"F1.wireOp",EDGE,"E871"),subQ1,subQ2,subQ3,subQ4])],"isStart":true})}),makeQuery(id+"F7.opExtrude","SWEPT_FACE",FACE,{"disambiguationData":[OSD([sQuery(id+"F6.wireOp",EDGE,"E909.MirrorCS")])]})]});}
            var Q7;
            {var subQ0=sQuery(id+"F1.wireOp",EDGE,"E868");var subQ1=sQuery(id+"F1.wireOp",EDGE,"E872");var subQ2=sQuery(id+"F1.wireOp",EDGE,"E873");var subQ3=sQuery(id+"F1.wireOp",EDGE,"E874");var subQ4=sQuery(id+"F1.wireOp",EDGE,"E875");Q7=makeQuery(id+"F7.boolean.opBoolean","INTERSECT",EDGE,{"derivedFrom":[makeQuery(id+"F3.boolean.opBoolean","SPLIT",FACE,{"disambiguationData":[TD([makeQuery(id+"F2.opExtrude","SWEPT_FACE",FACE,{"disambiguationData":[OSD([sQuery(id+"F0.wireOp",EDGE,"E0")])]})])],"derivedFrom":makeQuery(id+"F3.opExtrude","CAP_FACE",FACE,{"disambiguationData":[OSD([subQ0,sQuery(id+"F1.wireOp",EDGE,"E869"),sQuery(id+"F1.wireOp",EDGE,"E870"),sQuery(id+"F1.wireOp",EDGE,"E871"),subQ1,subQ2,subQ3,subQ4])],"isStart":true})}),makeQuery(id+"F7.opExtrude","SWEPT_FACE",FACE,{"disambiguationData":[OSD([sQuery(id+"F6.wireOp",EDGE,"E908.MirrorCS")])]})]});}
            var Q8;
            {var subQ0=sQuery(id+"F1.wireOp",EDGE,"E868");var subQ1=sQuery(id+"F1.wireOp",EDGE,"E872");var subQ2=sQuery(id+"F1.wireOp",EDGE,"E873");var subQ3=sQuery(id+"F1.wireOp",EDGE,"E874");var subQ4=sQuery(id+"F1.wireOp",EDGE,"E875");Q8=makeQuery(id+"F7.boolean.opBoolean","INTERSECT",EDGE,{"derivedFrom":[makeQuery(id+"F3.boolean.opBoolean","SPLIT",FACE,{"disambiguationData":[TD([makeQuery(id+"F2.opExtrude","SWEPT_FACE",FACE,{"disambiguationData":[OSD([sQuery(id+"F0.wireOp",EDGE,"E0")])]})])],"derivedFrom":makeQuery(id+"F3.opExtrude","CAP_FACE",FACE,{"disambiguationData":[OSD([subQ0,sQuery(id+"F1.wireOp",EDGE,"E869"),sQuery(id+"F1.wireOp",EDGE,"E870"),sQuery(id+"F1.wireOp",EDGE,"E871"),subQ1,subQ2,subQ3,subQ4])],"isStart":true})}),makeQuery(id+"F7.opExtrude","SWEPT_FACE",FACE,{"disambiguationData":[OSD([sQuery(id+"F6.wireOp",EDGE,"E907.MirrorCS")])]})]});}
            fillet(context, id + "F8", {"entities" : qUnion([Q0, Q1, Q2, Q3, Q4, Q5, Q6, Q7, Q8]), "radius" : 0.38 * mm, "tangentPropagation" : true, "allowEdgeOverflow" : false});
        }
        {
            var Q0;
            Q0=makeQuery(id+"F5.boolean.opBoolean","MERGE",FACE,{"derivedFrom":[makeQuery(id+"F2.opExtrude","CAP_FACE",FACE,{"disambiguationData":[OSD([sQuery(id+"F0.wireOp",EDGE,"E0"),sQuery(id+"F0.wireOp",EDGE,"E1"),sQuery(id+"F0.wireOp",EDGE,"E2"),sQuery(id+"F0.wireOp",EDGE,"E3"),sQuery(id+"F0.wireOp",EDGE,"E4"),sQuery(id+"F0.wireOp",EDGE,"E8"),sQuery(id+"F0.wireOp",EDGE,"E9"),sQuery(id+"F0.wireOp",EDGE,"E10"),sQuery(id+"F0.wireOp",EDGE,"E11"),sQuery(id+"F0.wireOp",EDGE,"E12"),sQuery(id+"F0.wireOp",EDGE,"E13"),sQuery(id+"F0.wireOp",EDGE,"E14"),sQuery(id+"F0.wireOp",EDGE,"E15"),sQuery(id+"F0.wireOp",EDGE,"E16"),sQuery(id+"F0.wireOp",EDGE,"E17"),sQuery(id+"F0.wireOp",EDGE,"E18"),sQuery(id+"F0.wireOp",EDGE,"E19"),sQuery(id+"F0.wireOp",EDGE,"E20"),sQuery(id+"F0.wireOp",EDGE,"E21"),sQuery(id+"F0.wireOp",EDGE,"E22"),sQuery(id+"F0.wireOp",EDGE,"E23"),sQuery(id+"F0.wireOp",EDGE,"E24"),sQuery(id+"F0.wireOp",EDGE,"E25"),sQuery(id+"F0.wireOp",EDGE,"E26"),sQuery(id+"F0.wireOp",EDGE,"E27"),sQuery(id+"F0.wireOp",EDGE,"E28"),sQuery(id+"F0.wireOp",EDGE,"E29"),sQuery(id+"F0.wireOp",EDGE,"E30"),sQuery(id+"F0.wireOp",EDGE,"E31"),sQuery(id+"F0.wireOp",EDGE,"E32"),sQuery(id+"F0.wireOp",EDGE,"E33"),sQuery(id+"F0.wireOp",EDGE,"E34"),sQuery(id+"F0.wireOp",EDGE,"E35"),sQuery(id+"F0.wireOp",EDGE,"E36"),sQuery(id+"F0.wireOp",EDGE,"E37"),sQuery(id+"F0.wireOp",EDGE,"E38"),sQuery(id+"F0.wireOp",EDGE,"E39"),sQuery(id+"F0.wireOp",EDGE,"E40"),sQuery(id+"F0.wireOp",EDGE,"E41"),sQuery(id+"F0.wireOp",EDGE,"E42"),sQuery(id+"F0.wireOp",EDGE,"E43"),sQuery(id+"F0.wireOp",EDGE,"E44"),sQuery(id+"F0.wireOp",EDGE,"E45"),sQuery(id+"F0.wireOp",EDGE,"E46"),sQuery(id+"F0.wireOp",EDGE,"E47"),sQuery(id+"F0.wireOp",EDGE,"E48"),sQuery(id+"F0.wireOp",EDGE,"E49"),sQuery(id+"F0.wireOp",EDGE,"E50"),sQuery(id+"F0.wireOp",EDGE,"E51"),sQuery(id+"F0.wireOp",EDGE,"E52"),sQuery(id+"F0.wireOp",EDGE,"E53"),sQuery(id+"F0.wireOp",EDGE,"E54"),sQuery(id+"F0.wireOp",EDGE,"E55"),sQuery(id+"F0.wireOp",EDGE,"E56"),sQuery(id+"F0.wireOp",EDGE,"E57"),sQuery(id+"F0.wireOp",EDGE,"E58"),sQuery(id+"F0.wireOp",EDGE,"E59"),sQuery(id+"F0.wireOp",EDGE,"E60"),sQuery(id+"F0.wireOp",EDGE,"E61"),sQuery(id+"F0.wireOp",EDGE,"E62"),sQuery(id+"F0.wireOp",EDGE,"E63")])],"isStart":false}),makeQuery(id+"F5.opExtrude","CAP_FACE",FACE,{"disambiguationData":[OSD([sQuery(id+"F4.wireOp",EDGE,"E881"),sQuery(id+"F4.wireOp",EDGE,"E882"),sQuery(id+"F4.wireOp",EDGE,"E883"),sQuery(id+"F4.wireOp",EDGE,"E884"),sQuery(id+"F4.wireOp",EDGE,"E885"),sQuery(id+"F4.wireOp",EDGE,"E886.1"),sQuery(id+"F4.wireOp",EDGE,"E886.2"),sQuery(id+"F4.wireOp",EDGE,"E886.3"),sQuery(id+"F4.wireOp",EDGE,"E888.filletArc"),sQuery(id+"F4.wireOp",EDGE,"E889.filletArc"),sQuery(id+"F4.wireOp",EDGE,"E891"),sQuery(id+"F4.wireOp",EDGE,"E892"),sQuery(id+"F4.wireOp",EDGE,"E893")])],"isStart":false})]});
            var sketch = newSketch(context, id + "F9", { "sketchPlane" : qUnion([Q0])});
            skText(sketch, "E910", { "text": "MENACING", "fontName": "OpenSans-Regular.ttf"});
            const initialGuessF9  = {"E910": [-0.01169, 0.02133, 1, 0, 0.00318]};
            skSetInitialGuess(sketch, initialGuessF9);
            skSolve(sketch);
        }
        {
            var Q0;
            Q0 = qSketchRegion(id + "F9", true);
            extrude(context, id + "F10", {"entities" : qUnion([Q0]), "operationType" : NewBodyOperationType.REMOVE, "oppositeDirection" : true, "depth" : 1.52 * mm, "offsetDistance" : 25.4 * mm});
        }
    });
